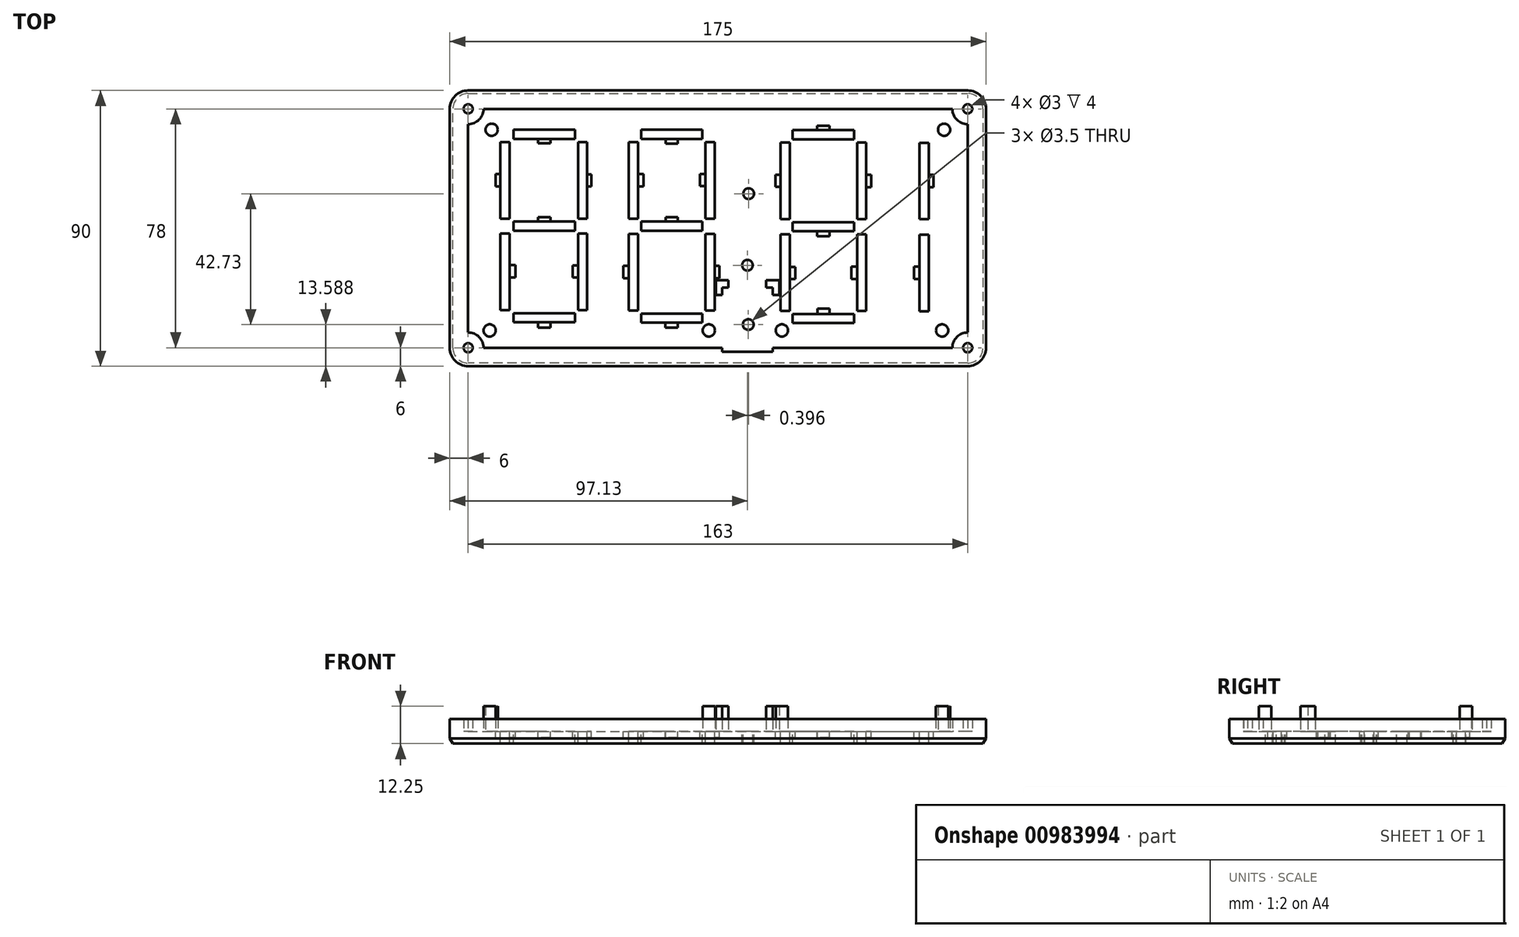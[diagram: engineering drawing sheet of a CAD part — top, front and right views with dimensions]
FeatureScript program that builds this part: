
annotation { "Feature Type Name" : "Feature", "Feature Type Description" : "" }
export const myFeature = defineFeature(function(context is Context, id is Id, definition is map)
    precondition{}
    {
        {
            var Q0;
            Q0=qCreatedBy(makeId("Top.planeOp"),FACE);
            var sketch = newSketch(context, id + "F0", { "sketchPlane" : qUnion([Q0])});
            skLineSegment(sketch, "E0.bottom", {"start": v(-87.5, 45) * mm, "end": v(87.5, 45) * mm});
            skLineSegment(sketch, "E0.top", {"start": v(-87.5, -45) * mm, "end": v(87.5, -45) * mm});
            skLineSegment(sketch, "E0.left", {"start": v(-87.5, 45) * mm, "end": v(-87.5, -45) * mm});
            skLineSegment(sketch, "E0.right", {"start": v(87.5, 45) * mm, "end": v(87.5, -45) * mm});
            skArc(sketch, "E1", {"start": v(-81.5, 34) * mm, "mid": v(-77.96, 35.46) * mm, "end": v(-76.5, 39) * mm});
            skArc(sketch, "E2", {"start": v(76.5, 39) * mm, "mid": v(77.96, 35.46) * mm, "end": v(81.5, 34) * mm});
            skArc(sketch, "E3", {"start": v(-76.5, -39) * mm, "mid": v(-77.96, -35.46) * mm, "end": v(-81.5, -34) * mm});
            skArc(sketch, "E4", {"start": v(81.5, -34) * mm, "mid": v(77.96, -35.46) * mm, "end": v(76.5, -39) * mm});
            skLineSegment(sketch, "E5", {"start": v(0, 39) * mm, "end": v(0, 0) * mm, "construction": true});
            skLineSegment(sketch, "E6.top", {"start": v(-68.01, -26.67) * mm, "end": v(-71.01, -26.67) * mm});
            skLineSegment(sketch, "E6.left", {"start": v(-68.01, -1.67) * mm, "end": v(-68.01, -26.67) * mm});
            skLineSegment(sketch, "E7.left", {"start": v(-68.01, 3.19) * mm, "end": v(-68.01, 28.19) * mm});
            skLineSegment(sketch, "E6.right", {"start": v(-71.01, -1.67) * mm, "end": v(-71.01, -26.67) * mm});
            skLineSegment(sketch, "E7.right", {"start": v(-71.01, 3.19) * mm, "end": v(-71.01, 28.19) * mm});
            skLineSegment(sketch, "E8.bottom", {"start": v(-45.68, -1.67) * mm, "end": v(-42.68, -1.67) * mm});
            skLineSegment(sketch, "E8.top", {"start": v(-45.68, -26.67) * mm, "end": v(-42.68, -26.67) * mm});
            skLineSegment(sketch, "E9.left", {"start": v(-46.68, 2.19) * mm, "end": v(-46.68, 29.19) * mm, "construction": true});
            skLineSegment(sketch, "E8.left", {"start": v(-45.68, -1.67) * mm, "end": v(-45.68, -26.67) * mm});
            skLineSegment(sketch, "E8.right", {"start": v(-42.68, -1.67) * mm, "end": v(-42.68, -26.67) * mm});
            skLineSegment(sketch, "E9.right", {"start": v(-41.68, 2.19) * mm, "end": v(-41.68, 29.19) * mm, "construction": true});
            skLineSegment(sketch, "E10", {"start": v(-45.68, -26.67) * mm, "end": v(-68.01, -26.67) * mm, "construction": true});
            skLineSegment(sketch, "E11.bottom", {"start": v(-46.68, -27.67) * mm, "end": v(-66.68, -27.67) * mm});
            skLineSegment(sketch, "E11.top", {"start": v(-46.68, -30.67) * mm, "end": v(-66.68, -30.67) * mm});
            skLineSegment(sketch, "E12.left", {"start": v(-66.68, 2.19) * mm, "end": v(-66.68, 29.19) * mm, "construction": true});
            skLineSegment(sketch, "E12.right", {"start": v(-72.01, 2.19) * mm, "end": v(-72.01, 29.19) * mm, "construction": true});
            skLineSegment(sketch, "E13.bottom", {"start": v(-46.68, 29.19) * mm, "end": v(-66.68, 29.19) * mm});
            skLineSegment(sketch, "E13.top", {"start": v(-46.68, 32.19) * mm, "end": v(-66.68, 32.19) * mm});
            skLineSegment(sketch, "E14.right", {"start": v(-42.68, 3.19) * mm, "end": v(-42.68, 28.19) * mm});
            skLineSegment(sketch, "E15.rect.bottom", {"start": v(-46.68, 2.19) * mm, "end": v(-66.68, 2.19) * mm});
            skLineSegment(sketch, "E15.rect.top", {"start": v(-46.68, -0.81) * mm, "end": v(-66.68, -0.81) * mm});
            skLineSegment(sketch, "E16.rect.bottom", {"start": v(-45.68, 3.19) * mm, "end": v(-68.01, 3.19) * mm, "construction": true});
            skLineSegment(sketch, "E16.rect.top", {"start": v(-45.68, -1.67) * mm, "end": v(-68.01, -1.67) * mm, "construction": true});
            skLineSegment(sketch, "E14.bottom", {"start": v(-45.68, 3.19) * mm, "end": v(-42.68, 3.19) * mm});
            skLineSegment(sketch, "E14.left", {"start": v(-45.68, 3.19) * mm, "end": v(-45.68, 28.19) * mm});
            skLineSegment(sketch, "E9.top", {"start": v(-46.68, 29.19) * mm, "end": v(-41.68, 29.19) * mm, "construction": true});
            skLineSegment(sketch, "E12.bottom", {"start": v(-66.68, 2.19) * mm, "end": v(-72.01, 2.19) * mm, "construction": true});
            skLineSegment(sketch, "E12.top", {"start": v(-66.68, 29.19) * mm, "end": v(-72.01, 29.19) * mm, "construction": true});
            skLineSegment(sketch, "E11.left", {"start": v(-46.68, -27.67) * mm, "end": v(-46.68, -30.67) * mm});
            skLineSegment(sketch, "E11.right", {"start": v(-66.68, -27.67) * mm, "end": v(-66.68, -30.67) * mm});
            skLineSegment(sketch, "E13.right", {"start": v(-66.68, 29.19) * mm, "end": v(-66.68, 32.19) * mm});
            skLineSegment(sketch, "E7.bottom", {"start": v(-68.01, 3.19) * mm, "end": v(-71.01, 3.19) * mm});
            skLineSegment(sketch, "E7.top", {"start": v(-68.01, 28.19) * mm, "end": v(-71.01, 28.19) * mm});
            skLineSegment(sketch, "E15.rect.left", {"start": v(-46.68, 2.19) * mm, "end": v(-46.68, -0.81) * mm});
            skLineSegment(sketch, "E15.rect.right", {"start": v(-66.68, 2.19) * mm, "end": v(-66.68, -0.81) * mm});
            skLineSegment(sketch, "E16.rect.right", {"start": v(-68.01, 3.19) * mm, "end": v(-68.01, -1.67) * mm, "construction": true});
            skLineSegment(sketch, "E13.left", {"start": v(-46.68, 29.19) * mm, "end": v(-46.68, 32.19) * mm});
            skLineSegment(sketch, "E14.top", {"start": v(-45.68, 28.19) * mm, "end": v(-42.68, 28.19) * mm});
            skLineSegment(sketch, "E6.bottom", {"start": v(-68.01, -1.67) * mm, "end": v(-71.01, -1.67) * mm});
            skLineSegment(sketch, "E9.bottom", {"start": v(-46.68, 2.19) * mm, "end": v(-41.68, 2.19) * mm, "construction": true});
            skLineSegment(sketch, "E16.rect.left", {"start": v(-45.68, 3.19) * mm, "end": v(-45.68, -1.67) * mm, "construction": true});
            skLineSegment(sketch, "E17.1.0.5", {"start": v(-5.06, -27.81) * mm, "end": v(-25.06, -27.81) * mm});
            skLineSegment(sketch, "E17.1.0.7", {"start": v(-4.06, -1.81) * mm, "end": v(-1.06, -1.81) * mm});
            skLineSegment(sketch, "E17.1.0.12", {"start": v(-4.06, 28.19) * mm, "end": v(-1.06, 28.19) * mm});
            skLineSegment(sketch, "E17.1.0.14", {"start": v(-4.06, 3.19) * mm, "end": v(-26.06, 3.19) * mm, "construction": true});
            skLineSegment(sketch, "E17.1.0.15", {"start": v(-26.06, -1.81) * mm, "end": v(-26.06, -26.81) * mm});
            skLineSegment(sketch, "E17.1.0.28", {"start": v(-5.06, -30.81) * mm, "end": v(-25.06, -30.81) * mm});
            skLineSegment(sketch, "E17.1.0.29", {"start": v(-1.06, -1.81) * mm, "end": v(-1.06, -26.81) * mm});
            skLineSegment(sketch, "E17.1.0.31", {"start": v(-4.06, -26.81) * mm, "end": v(-1.06, -26.81) * mm});
            skLineSegment(sketch, "E17.1.0.34", {"start": v(-26.06, 28.19) * mm, "end": v(-29.06, 28.19) * mm});
            skLineSegment(sketch, "E17.1.0.35", {"start": v(-5.06, 29.19) * mm, "end": v(-25.06, 29.19) * mm});
            skLineSegment(sketch, "E17.1.0.36", {"start": v(-29.06, -1.81) * mm, "end": v(-29.06, -26.81) * mm});
            skLineSegment(sketch, "E17.1.0.38", {"start": v(-5.06, 2.19) * mm, "end": v(-25.06, 2.19) * mm});
            skLineSegment(sketch, "E17.1.0.39", {"start": v(-26.06, -1.81) * mm, "end": v(-29.06, -1.81) * mm});
            skLineSegment(sketch, "E17.1.0.50", {"start": v(-4.06, -26.81) * mm, "end": v(-26.06, -26.81) * mm, "construction": true});
            skLineSegment(sketch, "E17.1.0.51", {"start": v(-4.06, -1.81) * mm, "end": v(-4.06, -26.81) * mm});
            skLineSegment(sketch, "E17.1.0.52", {"start": v(-5.06, 2.19) * mm, "end": v(-5.06, -0.81) * mm});
            skLineSegment(sketch, "E17.1.0.53", {"start": v(-4.06, 3.19) * mm, "end": v(-4.06, 28.19) * mm});
            skLineSegment(sketch, "E17.1.0.54", {"start": v(-5.06, 32.19) * mm, "end": v(-25.06, 32.19) * mm});
            skLineSegment(sketch, "E17.1.0.55", {"start": v(-29.06, 3.19) * mm, "end": v(-29.06, 28.19) * mm});
            skLineSegment(sketch, "E17.1.0.57", {"start": v(-30.06, 2.19) * mm, "end": v(-30.06, 29.19) * mm, "construction": true});
            skLineSegment(sketch, "E17.1.0.58", {"start": v(-4.06, -1.81) * mm, "end": v(-26.06, -1.81) * mm, "construction": true});
            skLineSegment(sketch, "E17.1.0.61", {"start": v(-26.06, 3.19) * mm, "end": v(-26.06, 28.19) * mm});
            skLineSegment(sketch, "E17.1.0.65", {"start": v(-25.06, 2.19) * mm, "end": v(-25.06, -0.81) * mm});
            skLineSegment(sketch, "E17.1.0.67", {"start": v(-1.06, 3.19) * mm, "end": v(-1.06, 28.19) * mm});
            skLineSegment(sketch, "E17.1.0.76", {"start": v(-25.06, 2.19) * mm, "end": v(-25.06, 29.19) * mm, "construction": true});
            skLineSegment(sketch, "E17.1.0.77", {"start": v(-5.06, -0.81) * mm, "end": v(-25.06, -0.81) * mm});
            skLineSegment(sketch, "E17.1.0.78", {"start": v(-0.06, 2.19) * mm, "end": v(-0.06, 29.19) * mm, "construction": true});
            skLineSegment(sketch, "E17.1.0.80", {"start": v(-5.06, 2.19) * mm, "end": v(-5.06, 29.19) * mm, "construction": true});
            skLineSegment(sketch, "E17.1.0.82", {"start": v(-5.06, -27.81) * mm, "end": v(-5.06, -30.81) * mm});
            skLineSegment(sketch, "E17.1.0.83", {"start": v(-26.06, -26.81) * mm, "end": v(-29.06, -26.81) * mm});
            skLineSegment(sketch, "E17.1.0.88", {"start": v(-5.06, 29.19) * mm, "end": v(-5.06, 32.19) * mm});
            skLineSegment(sketch, "E17.1.0.90", {"start": v(-25.06, -27.81) * mm, "end": v(-25.06, -30.81) * mm});
            skLineSegment(sketch, "E17.1.0.91", {"start": v(-5.06, 29.19) * mm, "end": v(-0.06, 29.19) * mm, "construction": true});
            skLineSegment(sketch, "E17.1.0.94", {"start": v(-5.06, 2.19) * mm, "end": v(-0.06, 2.19) * mm, "construction": true});
            skLineSegment(sketch, "E17.1.0.96", {"start": v(-4.06, 3.19) * mm, "end": v(-1.06, 3.19) * mm});
            skLineSegment(sketch, "E17.1.0.99", {"start": v(-26.06, 3.19) * mm, "end": v(-26.06, -1.81) * mm, "construction": true});
            skLineSegment(sketch, "E17.1.0.103", {"start": v(-26.06, 3.19) * mm, "end": v(-29.06, 3.19) * mm});
            skLineSegment(sketch, "E17.1.0.104", {"start": v(-25.06, 29.19) * mm, "end": v(-30.06, 29.19) * mm, "construction": true});
            skLineSegment(sketch, "E17.1.0.110", {"start": v(-25.06, 29.19) * mm, "end": v(-25.06, 32.19) * mm});
            skLineSegment(sketch, "E17.1.0.111", {"start": v(-25.06, 2.19) * mm, "end": v(-30.06, 2.19) * mm, "construction": true});
            skLineSegment(sketch, "E17.1.0.115", {"start": v(-4.06, 3.19) * mm, "end": v(-4.06, -1.81) * mm, "construction": true});
            skLineSegment(sketch, "E17.direction1", {"start": v(-42.68, 3.19) * mm, "end": v(-7.01, 3.19) * mm, "construction": true});
            skLineSegment(sketch, "E18.1.0.5", {"start": v(44.4, -27.96) * mm, "end": v(24.4, -27.96) * mm});
            skLineSegment(sketch, "E18.1.0.28", {"start": v(44.4, -30.96) * mm, "end": v(24.4, -30.96) * mm});
            skLineSegment(sketch, "E18.1.0.61", {"start": v(23.4, 3.04) * mm, "end": v(23.4, 28.04) * mm});
            skLineSegment(sketch, "E18.1.0.78", {"start": v(49.4, 2.04) * mm, "end": v(49.4, 29.04) * mm, "construction": true});
            skLineSegment(sketch, "E18.1.0.54", {"start": v(44.4, 32.04) * mm, "end": v(24.4, 32.04) * mm});
            skLineSegment(sketch, "E18.1.0.36", {"start": v(20.4, -1.96) * mm, "end": v(20.4, -26.96) * mm});
            skLineSegment(sketch, "E18.1.0.38", {"start": v(44.4, 2.04) * mm, "end": v(24.4, 2.04) * mm});
            skLineSegment(sketch, "E18.1.0.35", {"start": v(44.4, 29.04) * mm, "end": v(24.4, 29.04) * mm});
            skLineSegment(sketch, "E18.1.0.77", {"start": v(44.4, -0.96) * mm, "end": v(24.4, -0.96) * mm});
            skLineSegment(sketch, "E18.1.0.55", {"start": v(20.4, 3.04) * mm, "end": v(20.4, 28.04) * mm});
            skLineSegment(sketch, "E18.1.0.57", {"start": v(19.4, 2.04) * mm, "end": v(19.4, 29.04) * mm, "construction": true});
            skLineSegment(sketch, "E18.1.0.80", {"start": v(44.4, 2.04) * mm, "end": v(44.4, 29.04) * mm, "construction": true});
            skLineSegment(sketch, "E18.1.0.53", {"start": v(45.4, 3.04) * mm, "end": v(45.4, 28.04) * mm});
            skLineSegment(sketch, "E18.1.0.51", {"start": v(45.4, -1.96) * mm, "end": v(45.4, -26.96) * mm});
            skLineSegment(sketch, "E18.1.0.29", {"start": v(48.4, -1.96) * mm, "end": v(48.4, -26.96) * mm});
            skLineSegment(sketch, "E18.1.0.76", {"start": v(24.4, 2.04) * mm, "end": v(24.4, 29.04) * mm, "construction": true});
            skLineSegment(sketch, "E18.1.0.67", {"start": v(48.4, 3.04) * mm, "end": v(48.4, 28.04) * mm});
            skLineSegment(sketch, "E18.1.0.50", {"start": v(45.4, -26.96) * mm, "end": v(23.4, -26.96) * mm, "construction": true});
            skLineSegment(sketch, "E18.1.0.58", {"start": v(45.4, -1.96) * mm, "end": v(23.4, -1.96) * mm, "construction": true});
            skLineSegment(sketch, "E18.1.0.15", {"start": v(23.4, -1.96) * mm, "end": v(23.4, -26.96) * mm});
            skLineSegment(sketch, "E18.1.0.14", {"start": v(45.4, 3.04) * mm, "end": v(23.4, 3.04) * mm, "construction": true});
            skLineSegment(sketch, "E18.1.0.12", {"start": v(45.4, 28.04) * mm, "end": v(48.4, 28.04) * mm});
            skLineSegment(sketch, "E18.1.0.91", {"start": v(44.4, 29.04) * mm, "end": v(49.4, 29.04) * mm, "construction": true});
            skLineSegment(sketch, "E18.1.0.90", {"start": v(24.4, -27.96) * mm, "end": v(24.4, -30.96) * mm});
            skLineSegment(sketch, "E18.1.0.111", {"start": v(24.4, 2.04) * mm, "end": v(19.4, 2.04) * mm, "construction": true});
            skLineSegment(sketch, "E18.1.0.34", {"start": v(23.4, 28.04) * mm, "end": v(20.4, 28.04) * mm});
            skLineSegment(sketch, "E18.1.0.104", {"start": v(24.4, 29.04) * mm, "end": v(19.4, 29.04) * mm, "construction": true});
            skLineSegment(sketch, "E18.1.0.82", {"start": v(44.4, -27.96) * mm, "end": v(44.4, -30.96) * mm});
            skLineSegment(sketch, "E18.1.0.94", {"start": v(44.4, 2.04) * mm, "end": v(49.4, 2.04) * mm, "construction": true});
            skLineSegment(sketch, "E18.1.0.31", {"start": v(45.4, -26.96) * mm, "end": v(48.4, -26.96) * mm});
            skLineSegment(sketch, "E18.1.0.83", {"start": v(23.4, -26.96) * mm, "end": v(20.4, -26.96) * mm});
            skLineSegment(sketch, "E18.1.0.88", {"start": v(44.4, 29.04) * mm, "end": v(44.4, 32.04) * mm});
            skLineSegment(sketch, "E18.1.0.96", {"start": v(45.4, 3.04) * mm, "end": v(48.4, 3.04) * mm});
            skLineSegment(sketch, "E18.1.0.103", {"start": v(23.4, 3.04) * mm, "end": v(20.4, 3.04) * mm});
            skLineSegment(sketch, "E18.1.0.99", {"start": v(23.4, 3.04) * mm, "end": v(23.4, -1.96) * mm, "construction": true});
            skLineSegment(sketch, "E18.1.0.7", {"start": v(45.4, -1.96) * mm, "end": v(48.4, -1.96) * mm});
            skLineSegment(sketch, "E18.1.0.115", {"start": v(45.4, 3.04) * mm, "end": v(45.4, -1.96) * mm, "construction": true});
            skLineSegment(sketch, "E18.1.0.52", {"start": v(44.4, 2.04) * mm, "end": v(44.4, -0.96) * mm});
            skLineSegment(sketch, "E18.1.0.110", {"start": v(24.4, 29.04) * mm, "end": v(24.4, 32.04) * mm});
            skLineSegment(sketch, "E18.1.0.65", {"start": v(24.4, 2.04) * mm, "end": v(24.4, -0.96) * mm});
            skLineSegment(sketch, "E18.1.0.39", {"start": v(23.4, -1.96) * mm, "end": v(20.4, -1.96) * mm});
            skLineSegment(sketch, "E19.1.0.51", {"start": v(65.76, -2.04) * mm, "end": v(65.76, -27.04) * mm});
            skLineSegment(sketch, "E19.1.0.29", {"start": v(68.76, -2.04) * mm, "end": v(68.76, -27.04) * mm});
            skLineSegment(sketch, "E19.1.0.53", {"start": v(65.76, 2.96) * mm, "end": v(65.76, 27.96) * mm});
            skLineSegment(sketch, "E19.1.0.78", {"start": v(69.76, 1.96) * mm, "end": v(69.76, 28.96) * mm, "construction": true});
            skLineSegment(sketch, "E19.1.0.67", {"start": v(68.76, 2.96) * mm, "end": v(68.76, 27.96) * mm});
            skLineSegment(sketch, "E19.1.0.80", {"start": v(64.76, 1.96) * mm, "end": v(64.76, 28.96) * mm, "construction": true});
            skLineSegment(sketch, "E19.1.0.31", {"start": v(65.76, -27.04) * mm, "end": v(68.76, -27.04) * mm});
            skLineSegment(sketch, "E19.1.0.96", {"start": v(65.76, 2.96) * mm, "end": v(68.76, 2.96) * mm});
            skLineSegment(sketch, "E19.1.0.12", {"start": v(65.76, 27.96) * mm, "end": v(68.76, 27.96) * mm});
            skLineSegment(sketch, "E19.1.0.94", {"start": v(64.76, 1.96) * mm, "end": v(69.76, 1.96) * mm, "construction": true});
            skLineSegment(sketch, "E19.1.0.7", {"start": v(65.76, -2.04) * mm, "end": v(68.76, -2.04) * mm});
            skLineSegment(sketch, "E19.1.0.91", {"start": v(64.76, 28.96) * mm, "end": v(69.76, 28.96) * mm, "construction": true});
            skLineSegment(sketch, "E19.1.0.115", {"start": v(65.76, 2.96) * mm, "end": v(65.76, -2.04) * mm, "construction": true});
            skLineSegment(sketch, "E20", {"start": v(-66.68, 32.19) * mm, "end": v(77.46, 32.19) * mm, "construction": true});
            skLineSegment(sketch, "E21", {"start": v(50.1, 29.04) * mm, "end": v(77.85, 29.04) * mm, "construction": true});
            skCircle(sketch, "E22", {"center": v(9.63, -12.05) * mm, "radius": 1.75 * mm});
            skCircle(sketch, "E23", {"center": v(10.03, 11.32) * mm, "radius": 1.75 * mm});
            skCircle(sketch, "E24", {"center": v(-81.5, 39) * mm, "radius": 1.5 * mm});
            skCircle(sketch, "E25", {"center": v(-81.5, -39) * mm, "radius": 1.5 * mm});
            skCircle(sketch, "E26", {"center": v(81.5, -39) * mm, "radius": 1.5 * mm});
            skCircle(sketch, "E27", {"center": v(81.5, 39) * mm, "radius": 1.5 * mm});
            skLineSegment(sketch, "E28.trimOffspring", {"start": v(81.5, 34) * mm, "end": v(81.5, -34) * mm});
            skLineSegment(sketch, "E29.trimOffspring", {"start": v(-76.5, -39) * mm, "end": v(17.9, -39) * mm});
            skLineSegment(sketch, "E30.trimOffspring", {"start": v(-81.5, 34) * mm, "end": v(-81.5, -34) * mm});
            skLineSegment(sketch, "E31.trimOffspring", {"start": v(-76.5, 39) * mm, "end": v(76.5, 39) * mm});
            skLineSegment(sketch, "E32.rect.bottom", {"start": v(17.9, -40.3) * mm, "end": v(1.4, -40.3) * mm});
            skLineSegment(sketch, "E32.rect.top", {"start": v(17.9, -19.35) * mm, "end": v(15.73, -19.35) * mm});
            skLineSegment(sketch, "E32.rect.left", {"start": v(17.9, -40.3) * mm, "end": v(17.9, -39) * mm});
            skLineSegment(sketch, "E32.rect.right", {"start": v(1.4, -40.3) * mm, "end": v(1.4, -39) * mm});
            skPoint(sketch, "E32.rect.middle", {"position": v(9.65, -29.82) * mm});
            skCircle(sketch, "E33", {"center": v(9.9, -31.41) * mm, "radius": 1.75 * mm});
            skLineSegment(sketch, "E34.rect.bottom", {"start": v(17.9, -21.72) * mm, "end": v(20.08, -21.72) * mm});
            skLineSegment(sketch, "E34.rect.top", {"start": v(15.73, -16.98) * mm, "end": v(20.08, -16.98) * mm});
            skLineSegment(sketch, "E34.rect.left", {"start": v(15.73, -19.35) * mm, "end": v(15.73, -16.98) * mm});
            skLineSegment(sketch, "E34.rect.right", {"start": v(20.08, -21.72) * mm, "end": v(20.08, -16.98) * mm});
            skPoint(sketch, "E34.rect.middle", {"position": v(17.9, -19.35) * mm});
            skLineSegment(sketch, "E35.rect.bottom", {"start": v(1.4, -21.72) * mm, "end": v(-0.6, -21.72) * mm});
            skLineSegment(sketch, "E35.rect.top", {"start": v(3.4, -16.98) * mm, "end": v(-0.6, -16.98) * mm});
            skLineSegment(sketch, "E35.rect.left", {"start": v(3.4, -19.35) * mm, "end": v(3.4, -16.98) * mm});
            skLineSegment(sketch, "E35.rect.right", {"start": v(-0.6, -21.72) * mm, "end": v(-0.6, -16.98) * mm});
            skPoint(sketch, "E35.rect.middle", {"position": v(1.4, -19.35) * mm});
            skPoint(sketch, "E36.orphan", {"position": v(3.4, -21.72) * mm});
            skPoint(sketch, "E37.orphan", {"position": v(15.73, -21.72) * mm});
            skLineSegment(sketch, "E38", {"start": v(3.4, -19.35) * mm, "end": v(1.4, -19.35) * mm});
            skLineSegment(sketch, "E39", {"start": v(15.73, -19.35) * mm, "end": v(3.4, -19.35) * mm, "construction": true});
            skLineSegment(sketch, "E40", {"start": v(1.4, -21.72) * mm, "end": v(1.4, -19.35) * mm});
            skLineSegment(sketch, "E41", {"start": v(17.9, -21.72) * mm, "end": v(17.9, -19.35) * mm});
            skLineSegment(sketch, "E42", {"start": v(17.9, -39) * mm, "end": v(76.5, -39) * mm});
            skLineSegment(sketch, "E43", {"start": v(1.4, -39) * mm, "end": v(1.4, -21.72) * mm, "construction": true});
            skLineSegment(sketch, "E44", {"start": v(17.9, -39) * mm, "end": v(17.9, -21.72) * mm, "construction": true});
            skCircle(sketch, "E45", {"center": v(73.8, 32.19) * mm, "radius": 2 * mm});
            skCircle(sketch, "E46", {"center": v(73.15, -33.33) * mm, "radius": 2 * mm});
            skCircle(sketch, "E47", {"center": v(-73.84, 32.19) * mm, "radius": 2 * mm});
            skCircle(sketch, "E48", {"center": v(-74.5, -33.33) * mm, "radius": 2 * mm});
            skCircle(sketch, "E49", {"center": v(20.87, -33.33) * mm, "radius": 2 * mm});
            skCircle(sketch, "E50", {"center": v(-2.98, -33.33) * mm, "radius": 2 * mm});
            skLineSegment(sketch, "E51.rect.bottom", {"start": v(-66.1, -16.02) * mm, "end": v(-68.01, -16.02) * mm});
            skLineSegment(sketch, "E51.rect.top", {"start": v(-66.1, -12.02) * mm, "end": v(-68.01, -12.02) * mm});
            skLineSegment(sketch, "E51.rect.left", {"start": v(-66.1, -16.02) * mm, "end": v(-66.1, -12.02) * mm});
            skLineSegment(sketch, "E52.rect.bottom", {"start": v(-47.39, -16.1) * mm, "end": v(-45.68, -16.1) * mm});
            skLineSegment(sketch, "E52.rect.top", {"start": v(-47.39, -12.1) * mm, "end": v(-45.68, -12.1) * mm});
            skLineSegment(sketch, "E52.rect.left", {"start": v(-47.39, -16.1) * mm, "end": v(-47.39, -12.1) * mm});
            skLineSegment(sketch, "E53.rect.bottom", {"start": v(-58.68, -32.37) * mm, "end": v(-54.68, -32.37) * mm});
            skLineSegment(sketch, "E53.rect.left", {"start": v(-58.68, -32.37) * mm, "end": v(-58.68, -30.67) * mm});
            skLineSegment(sketch, "E53.rect.right", {"start": v(-54.68, -32.37) * mm, "end": v(-54.68, -30.67) * mm});
            skLineSegment(sketch, "E54.rect.bottom", {"start": v(-58.68, 3.68) * mm, "end": v(-54.68, 3.68) * mm});
            skLineSegment(sketch, "E54.rect.left", {"start": v(-58.68, 3.68) * mm, "end": v(-58.68, 2.19) * mm});
            skLineSegment(sketch, "E54.rect.right", {"start": v(-54.68, 3.68) * mm, "end": v(-54.68, 2.19) * mm});
            skLineSegment(sketch, "E55.rect.bottom", {"start": v(-72.53, 13.69) * mm, "end": v(-71.01, 13.69) * mm});
            skLineSegment(sketch, "E55.rect.top", {"start": v(-72.53, 17.69) * mm, "end": v(-71.01, 17.69) * mm});
            skLineSegment(sketch, "E55.rect.left", {"start": v(-72.53, 13.69) * mm, "end": v(-72.53, 17.69) * mm});
            skLineSegment(sketch, "E56.rect.bottom", {"start": v(-58.68, 27.77) * mm, "end": v(-54.68, 27.77) * mm});
            skLineSegment(sketch, "E56.rect.left", {"start": v(-58.68, 27.77) * mm, "end": v(-58.68, 29.19) * mm});
            skLineSegment(sketch, "E56.rect.right", {"start": v(-54.68, 27.77) * mm, "end": v(-54.68, 29.19) * mm});
            skLineSegment(sketch, "E57.rect.bottom", {"start": v(-41.3, 17.68) * mm, "end": v(-42.68, 17.68) * mm});
            skLineSegment(sketch, "E57.rect.top", {"start": v(-41.3, 13.68) * mm, "end": v(-42.68, 13.68) * mm});
            skLineSegment(sketch, "E57.rect.left", {"start": v(-41.3, 17.68) * mm, "end": v(-41.3, 13.68) * mm});
            skLineSegment(sketch, "E58.rect.bottom", {"start": v(-17.1, 27.61) * mm, "end": v(-13.1, 27.61) * mm});
            skLineSegment(sketch, "E58.rect.left", {"start": v(-17.1, 27.61) * mm, "end": v(-17.1, 29.19) * mm});
            skLineSegment(sketch, "E58.rect.right", {"start": v(-13.1, 27.61) * mm, "end": v(-13.1, 29.19) * mm});
            skLineSegment(sketch, "E59.rect.bottom", {"start": v(-24.23, 17.69) * mm, "end": v(-26.06, 17.69) * mm});
            skLineSegment(sketch, "E59.rect.top", {"start": v(-24.23, 13.69) * mm, "end": v(-26.06, 13.69) * mm});
            skLineSegment(sketch, "E59.rect.left", {"start": v(-24.23, 17.69) * mm, "end": v(-24.23, 13.69) * mm});
            skLineSegment(sketch, "E60.rect.bottom", {"start": v(-5.85, 13.78) * mm, "end": v(-4.06, 13.78) * mm});
            skLineSegment(sketch, "E60.rect.top", {"start": v(-5.85, 17.78) * mm, "end": v(-4.06, 17.78) * mm});
            skLineSegment(sketch, "E60.rect.left", {"start": v(-5.85, 13.78) * mm, "end": v(-5.85, 17.78) * mm});
            skLineSegment(sketch, "E61.rect.bottom", {"start": v(-17.1, 3.6) * mm, "end": v(-13.1, 3.6) * mm});
            skLineSegment(sketch, "E61.rect.left", {"start": v(-17.1, 3.6) * mm, "end": v(-17.1, 2.19) * mm});
            skLineSegment(sketch, "E61.rect.right", {"start": v(-13.1, 3.6) * mm, "end": v(-13.1, 2.19) * mm});
            skLineSegment(sketch, "E62.rect.bottom", {"start": v(-30.88, -12.29) * mm, "end": v(-29.06, -12.29) * mm});
            skLineSegment(sketch, "E62.rect.top", {"start": v(-30.88, -16.29) * mm, "end": v(-29.06, -16.29) * mm});
            skLineSegment(sketch, "E62.rect.left", {"start": v(-30.88, -12.29) * mm, "end": v(-30.88, -16.29) * mm});
            skLineSegment(sketch, "E63.rect.bottom", {"start": v(0.5, -12.23) * mm, "end": v(-1.06, -12.23) * mm});
            skLineSegment(sketch, "E63.rect.top", {"start": v(0.5, -16.23) * mm, "end": v(-1.06, -16.23) * mm});
            skLineSegment(sketch, "E63.rect.left", {"start": v(0.5, -12.23) * mm, "end": v(0.5, -16.23) * mm});
            skLineSegment(sketch, "E64.rect.bottom", {"start": v(-17.16, -32.42) * mm, "end": v(-13.16, -32.42) * mm});
            skLineSegment(sketch, "E64.rect.left", {"start": v(-17.16, -32.42) * mm, "end": v(-17.16, -30.81) * mm});
            skLineSegment(sketch, "E64.rect.right", {"start": v(-13.16, -32.42) * mm, "end": v(-13.16, -30.81) * mm});
            skLineSegment(sketch, "E65.rect.bottom", {"start": v(32.4, 33.52) * mm, "end": v(36.4, 33.52) * mm});
            skLineSegment(sketch, "E65.rect.left", {"start": v(32.4, 33.52) * mm, "end": v(32.4, 32.04) * mm});
            skLineSegment(sketch, "E65.rect.right", {"start": v(36.4, 33.52) * mm, "end": v(36.4, 32.04) * mm});
            skLineSegment(sketch, "E66.rect.bottom", {"start": v(18.75, 13.55) * mm, "end": v(20.4, 13.55) * mm});
            skLineSegment(sketch, "E66.rect.top", {"start": v(18.75, 17.55) * mm, "end": v(20.4, 17.55) * mm});
            skLineSegment(sketch, "E66.rect.left", {"start": v(18.75, 13.55) * mm, "end": v(18.75, 17.55) * mm});
            skLineSegment(sketch, "E67.rect.bottom", {"start": v(50, 17.48) * mm, "end": v(48.4, 17.48) * mm});
            skLineSegment(sketch, "E67.rect.top", {"start": v(50, 13.48) * mm, "end": v(48.4, 13.48) * mm});
            skLineSegment(sketch, "E67.rect.left", {"start": v(50, 17.48) * mm, "end": v(50, 13.48) * mm});
            skLineSegment(sketch, "E68.rect.bottom", {"start": v(32.38, -2.53) * mm, "end": v(36.38, -2.53) * mm});
            skLineSegment(sketch, "E68.rect.left", {"start": v(32.38, -2.53) * mm, "end": v(32.38, -0.96) * mm});
            skLineSegment(sketch, "E68.rect.right", {"start": v(36.38, -2.53) * mm, "end": v(36.38, -0.96) * mm});
            skLineSegment(sketch, "E69.rect.bottom", {"start": v(25.28, -12.57) * mm, "end": v(23.4, -12.57) * mm});
            skLineSegment(sketch, "E69.rect.top", {"start": v(25.28, -16.57) * mm, "end": v(23.4, -16.57) * mm});
            skLineSegment(sketch, "E69.rect.left", {"start": v(25.28, -12.57) * mm, "end": v(25.28, -16.57) * mm});
            skLineSegment(sketch, "E70.rect.bottom", {"start": v(43.49, -16.54) * mm, "end": v(45.4, -16.54) * mm});
            skLineSegment(sketch, "E70.rect.top", {"start": v(43.49, -12.54) * mm, "end": v(45.4, -12.54) * mm});
            skLineSegment(sketch, "E70.rect.left", {"start": v(43.49, -16.54) * mm, "end": v(43.49, -12.54) * mm});
            skLineSegment(sketch, "E71.rect.bottom", {"start": v(36.43, -26.21) * mm, "end": v(32.43, -26.21) * mm});
            skLineSegment(sketch, "E71.rect.left", {"start": v(36.43, -26.21) * mm, "end": v(36.43, -27.96) * mm});
            skLineSegment(sketch, "E71.rect.right", {"start": v(32.43, -26.21) * mm, "end": v(32.43, -27.96) * mm});
            skLineSegment(sketch, "E72.rect.bottom", {"start": v(68.76, 17.48) * mm, "end": v(70.36, 17.48) * mm});
            skLineSegment(sketch, "E72.rect.top", {"start": v(68.76, 13.45) * mm, "end": v(70.36, 13.45) * mm});
            skLineSegment(sketch, "E72.rect.right", {"start": v(70.36, 17.48) * mm, "end": v(70.36, 13.45) * mm});
            skLineSegment(sketch, "E73.rect.bottom", {"start": v(63.96, -12.54) * mm, "end": v(65.76, -12.54) * mm});
            skLineSegment(sketch, "E73.rect.top", {"start": v(63.96, -16.53) * mm, "end": v(65.76, -16.53) * mm});
            skLineSegment(sketch, "E73.rect.left", {"start": v(63.96, -12.54) * mm, "end": v(63.96, -16.53) * mm});
            skSolve(sketch);
        }
        {
            var Q0;
            Q0=makeQuery(id+"F0.imprint","IMPRINT",FACE,{"disambiguationData":[TD([[makeQuery(id+"F0.imprint","IMPRINT",EDGE,{"derivedFrom":sQuery(id+"F0.wireOp",EDGE,"E0.bottom")}),-1.0]])]});
            var Q1;
            Q1=makeQuery(id+"F0.imprint","IMPRINT",FACE,{"disambiguationData":[TD([[makeQuery(id+"F0.imprint","IMPRINT",EDGE,{"derivedFrom":sQuery(id+"F0.wireOp",EDGE,"E17.1.0.5")}),1.0]])]});
            var Q2;
            {var subQ7=sQuery(id+"F0.wireOp",EDGE,"E17.1.0.12");Q2=makeQuery(id+"F0.imprint","IMPRINT",FACE,{"disambiguationData":[TD([[makeQuery(id+"F0.imprint","IMPRINT",EDGE,{"derivedFrom":subQ7}),-1.0]])]});}
            var Q3;
            {var subQ7=sQuery(id+"F0.wireOp",EDGE,"E17.1.0.7");Q3=makeQuery(id+"F0.imprint","IMPRINT",FACE,{"disambiguationData":[TD([[makeQuery(id+"F0.imprint","IMPRINT",EDGE,{"derivedFrom":subQ7}),-1.0]])]});}
            var Q4;
            Q4=makeQuery(id+"F0.imprint","IMPRINT",FACE,{"disambiguationData":[TD([[makeQuery(id+"F0.imprint","IMPRINT",EDGE,{"derivedFrom":sQuery(id+"F0.wireOp",EDGE,"E11.bottom")}),1.0]])]});
            var Q5;
            Q5=makeQuery(id+"F0.imprint","IMPRINT",FACE,{"disambiguationData":[TD([[makeQuery(id+"F0.imprint","IMPRINT",EDGE,{"derivedFrom":sQuery(id+"F0.wireOp",EDGE,"E18.1.0.38")}),1.0]])]});
            var Q6;
            Q6=makeQuery(id+"F0.imprint","IMPRINT",FACE,{"disambiguationData":[TD([[makeQuery(id+"F0.imprint","IMPRINT",EDGE,{"derivedFrom":sQuery(id+"F0.wireOp",EDGE,"E18.1.0.29")}),-1.0]])]});
            var Q7;
            Q7=makeQuery(id+"F0.imprint","IMPRINT",FACE,{"disambiguationData":[TD([[makeQuery(id+"F0.imprint","IMPRINT",EDGE,{"derivedFrom":sQuery(id+"F0.wireOp",EDGE,"E18.1.0.28")}),-1.0]])]});
            var Q8;
            {var subQ7=sQuery(id+"F0.wireOp",EDGE,"E6.top");Q8=makeQuery(id+"F0.imprint","IMPRINT",FACE,{"disambiguationData":[TD([[makeQuery(id+"F0.imprint","IMPRINT",EDGE,{"derivedFrom":subQ7}),-1.0]])]});}
            var Q9;
            Q9=makeQuery(id+"F0.imprint","IMPRINT",FACE,{"disambiguationData":[TD([[makeQuery(id+"F0.imprint","IMPRINT",EDGE,{"derivedFrom":sQuery(id+"F0.wireOp",EDGE,"E7.left")}),1.0]])]});
            var Q10;
            {var subQ7=sQuery(id+"F0.wireOp",EDGE,"E8.bottom");Q10=makeQuery(id+"F0.imprint","IMPRINT",FACE,{"disambiguationData":[TD([[makeQuery(id+"F0.imprint","IMPRINT",EDGE,{"derivedFrom":subQ7}),-1.0]])]});}
            var Q11;
            Q11=makeQuery(id+"F0.imprint","IMPRINT",FACE,{"disambiguationData":[TD([[makeQuery(id+"F0.imprint","IMPRINT",EDGE,{"derivedFrom":sQuery(id+"F0.wireOp",EDGE,"E13.top")}),1.0]])]});
            var Q12;
            {var subQ7=sQuery(id+"F0.wireOp",EDGE,"E14.bottom");Q12=makeQuery(id+"F0.imprint","IMPRINT",FACE,{"disambiguationData":[TD([[makeQuery(id+"F0.imprint","IMPRINT",EDGE,{"derivedFrom":subQ7}),1.0]])]});}
            var Q13;
            Q13=makeQuery(id+"F0.imprint","IMPRINT",FACE,{"disambiguationData":[TD([[makeQuery(id+"F0.imprint","IMPRINT",EDGE,{"derivedFrom":sQuery(id+"F0.wireOp",EDGE,"E15.rect.top")}),-1.0]])]});
            var Q14;
            Q14=makeQuery(id+"F0.imprint","IMPRINT",FACE,{"disambiguationData":[TD([[makeQuery(id+"F0.imprint","IMPRINT",EDGE,{"derivedFrom":sQuery(id+"F0.wireOp",EDGE,"E19.1.0.53")}),-1.0]])]});
            var Q15;
            Q15=makeQuery(id+"F0.imprint","IMPRINT",FACE,{"disambiguationData":[TD([[makeQuery(id+"F0.imprint","IMPRINT",EDGE,{"derivedFrom":sQuery(id+"F0.wireOp",EDGE,"E18.1.0.61")}),1.0]])]});
            var Q16;
            {var subQ7=sQuery(id+"F0.wireOp",EDGE,"E17.1.0.52");Q16=makeQuery(id+"F0.imprint","IMPRINT",FACE,{"disambiguationData":[TD([[makeQuery(id+"F0.imprint","IMPRINT",EDGE,{"derivedFrom":subQ7}),-1.0]])]});}
            var Q17;
            Q17=makeQuery(id+"F0.imprint","IMPRINT",FACE,{"disambiguationData":[TD([[makeQuery(id+"F0.imprint","IMPRINT",EDGE,{"derivedFrom":sQuery(id+"F0.wireOp",EDGE,"E1")}),-1.0]])]});
            var Q18;
            Q18=makeQuery(id+"F0.imprint","IMPRINT",FACE,{"disambiguationData":[TD([[makeQuery(id+"F0.imprint","IMPRINT",EDGE,{"derivedFrom":sQuery(id+"F0.wireOp",EDGE,"E18.1.0.36")}),1.0]])]});
            var Q19;
            Q19=makeQuery(id+"F0.imprint","IMPRINT",FACE,{"disambiguationData":[TD([[makeQuery(id+"F0.imprint","IMPRINT",EDGE,{"derivedFrom":sQuery(id+"F0.wireOp",EDGE,"E17.1.0.54")}),1.0]])]});
            var Q20;
            Q20=makeQuery(id+"F0.imprint","IMPRINT",FACE,{"disambiguationData":[TD([[makeQuery(id+"F0.imprint","IMPRINT",EDGE,{"derivedFrom":sQuery(id+"F0.wireOp",EDGE,"E19.1.0.29")}),-1.0]])]});
            var Q21;
            Q21=makeQuery(id+"F0.imprint","IMPRINT",FACE,{"disambiguationData":[TD([[makeQuery(id+"F0.imprint","IMPRINT",EDGE,{"derivedFrom":sQuery(id+"F0.wireOp",EDGE,"E17.1.0.15")}),-1.0]])]});
            var Q22;
            {var subQ6=sQuery(id+"F0.wireOp",EDGE,"E17.1.0.34");Q22=makeQuery(id+"F0.imprint","IMPRINT",FACE,{"disambiguationData":[TD([[makeQuery(id+"F0.imprint","IMPRINT",EDGE,{"derivedFrom":subQ6}),1.0]])]});}
            var Q23;
            Q23=makeQuery(id+"F0.imprint","IMPRINT",FACE,{"disambiguationData":[TD([[makeQuery(id+"F0.imprint","IMPRINT",EDGE,{"derivedFrom":sQuery(id+"F0.wireOp",EDGE,"E18.1.0.53")}),-1.0]])]});
            var Q24;
            Q24=makeQuery(id+"F0.imprint","IMPRINT",FACE,{"disambiguationData":[TD([[makeQuery(id+"F0.imprint","IMPRINT",EDGE,{"derivedFrom":sQuery(id+"F0.wireOp",EDGE,"E18.1.0.35")}),-1.0]])]});
            var Q25;
            Q25=makeQuery(id+"F0.imprint","IMPRINT",FACE,{"disambiguationData":[TD([[makeQuery(id+"F0.imprint","IMPRINT",EDGE,{"derivedFrom":sQuery(id+"F0.wireOp",EDGE,"E22")}),1.0]])]});
            var Q26;
            Q26=makeQuery(id+"F0.imprint","IMPRINT",FACE,{"disambiguationData":[TD([[makeQuery(id+"F0.imprint","IMPRINT",EDGE,{"derivedFrom":sQuery(id+"F0.wireOp",EDGE,"E23")}),1.0]])]});
            var Q27;
            Q27=makeQuery(id+"F0.imprint","IMPRINT",FACE,{"disambiguationData":[TD([[makeQuery(id+"F0.imprint","IMPRINT",EDGE,{"derivedFrom":sQuery(id+"F0.wireOp",EDGE,"E24")}),1.0]])]});
            var Q28;
            Q28=makeQuery(id+"F0.imprint","IMPRINT",FACE,{"disambiguationData":[TD([[makeQuery(id+"F0.imprint","IMPRINT",EDGE,{"derivedFrom":sQuery(id+"F0.wireOp",EDGE,"E25")}),1.0]])]});
            var Q29;
            Q29=makeQuery(id+"F0.imprint","IMPRINT",FACE,{"disambiguationData":[TD([[makeQuery(id+"F0.imprint","IMPRINT",EDGE,{"derivedFrom":sQuery(id+"F0.wireOp",EDGE,"E26")}),1.0]])]});
            var Q30;
            Q30=makeQuery(id+"F0.imprint","IMPRINT",FACE,{"disambiguationData":[TD([[makeQuery(id+"F0.imprint","IMPRINT",EDGE,{"derivedFrom":sQuery(id+"F0.wireOp",EDGE,"E27")}),1.0]])]});
            var Q31;
            {var subQ3=sQuery(id+"F0.wireOp",EDGE,"d27d8e91-9dc8-4657-a3bc-17c214d1fbd1.rect.top");Q31=makeQuery(id+"F0.imprint","IMPRINT",FACE,{"disambiguationData":[TD([[makeQuery(id+"F0.imprint","IMPRINT",EDGE,{"derivedFrom":subQ3}),1.0]])]});}
            var Q32;
            {var subQ3=sQuery(id+"F0.wireOp",EDGE,"d27d8e91-9dc8-4657-a3bc-17c214d1fbd1.rect.bottom");Q32=makeQuery(id+"F0.imprint","IMPRINT",FACE,{"disambiguationData":[TD([[makeQuery(id+"F0.imprint","IMPRINT",EDGE,{"derivedFrom":subQ3}),-1.0]])]});}
            var Q33;
            {var subQ0=sQuery(id+"F0.wireOp",EDGE,"11542846-51ec-4e1d-9889-e9b2482069cd.rect.left");Q33=makeQuery(id+"F0.imprint","IMPRINT",FACE,{"disambiguationData":[TD([[makeQuery(id+"F0.imprint","IMPRINT",EDGE,{"derivedFrom":subQ0}),-1.0]])]});}
            var Q34;
            {var subQ0=sQuery(id+"F0.wireOp",EDGE,"11542846-51ec-4e1d-9889-e9b2482069cd.rect.right");Q34=makeQuery(id+"F0.imprint","IMPRINT",FACE,{"disambiguationData":[TD([[makeQuery(id+"F0.imprint","IMPRINT",EDGE,{"derivedFrom":subQ0}),1.0]])]});}
            var Q35;
            {var subQ0=sQuery(id+"F0.wireOp",EDGE,"7a176b9b-9b07-41be-aea8-fdd94f8c28c8.rect.right");Q35=makeQuery(id+"F0.imprint","IMPRINT",FACE,{"disambiguationData":[TD([[makeQuery(id+"F0.imprint","IMPRINT",EDGE,{"derivedFrom":subQ0}),1.0]])]});}
            var Q36;
            {var subQ0=sQuery(id+"F0.wireOp",EDGE,"7a176b9b-9b07-41be-aea8-fdd94f8c28c8.rect.left");Q36=makeQuery(id+"F0.imprint","IMPRINT",FACE,{"disambiguationData":[TD([[makeQuery(id+"F0.imprint","IMPRINT",EDGE,{"derivedFrom":subQ0}),-1.0]])]});}
            var Q37;
            {var subQ0=sQuery(id+"F0.wireOp",EDGE,"7fec9149-b94b-4e31-a2bc-72143b81982d.rect.right");Q37=makeQuery(id+"F0.imprint","IMPRINT",FACE,{"disambiguationData":[TD([[makeQuery(id+"F0.imprint","IMPRINT",EDGE,{"derivedFrom":subQ0}),-1.0]])]});}
            var Q38;
            {var subQ0=sQuery(id+"F0.wireOp",EDGE,"7fec9149-b94b-4e31-a2bc-72143b81982d.rect.left");Q38=makeQuery(id+"F0.imprint","IMPRINT",FACE,{"disambiguationData":[TD([[makeQuery(id+"F0.imprint","IMPRINT",EDGE,{"derivedFrom":subQ0}),1.0]])]});}
            var Q39;
            {var subQ3=sQuery(id+"F0.wireOp",EDGE,"2390580b-736b-4805-a3aa-b3ade61d923c.rect.bottom");Q39=makeQuery(id+"F0.imprint","IMPRINT",FACE,{"disambiguationData":[TD([[makeQuery(id+"F0.imprint","IMPRINT",EDGE,{"derivedFrom":subQ3}),1.0]])]});}
            var Q40;
            {var subQ3=sQuery(id+"F0.wireOp",EDGE,"2390580b-736b-4805-a3aa-b3ade61d923c.rect.top");Q40=makeQuery(id+"F0.imprint","IMPRINT",FACE,{"disambiguationData":[TD([[makeQuery(id+"F0.imprint","IMPRINT",EDGE,{"derivedFrom":subQ3}),-1.0]])]});}
            var Q41;
            {var subQ0=sQuery(id+"F0.wireOp",EDGE,"2166e6f4-a4c2-4c34-8466-9477065b0f98.rect.left");Q41=makeQuery(id+"F0.imprint","IMPRINT",FACE,{"disambiguationData":[TD([[makeQuery(id+"F0.imprint","IMPRINT",EDGE,{"derivedFrom":subQ0}),1.0]])]});}
            var Q42;
            {var subQ0=sQuery(id+"F0.wireOp",EDGE,"2166e6f4-a4c2-4c34-8466-9477065b0f98.rect.right");Q42=makeQuery(id+"F0.imprint","IMPRINT",FACE,{"disambiguationData":[TD([[makeQuery(id+"F0.imprint","IMPRINT",EDGE,{"derivedFrom":subQ0}),-1.0]])]});}
            var Q43;
            {var subQ3=sQuery(id+"F0.wireOp",EDGE,"a0b229e6-3aa1-4465-9a5a-0985d3e63f01.rect.top");Q43=makeQuery(id+"F0.imprint","IMPRINT",FACE,{"disambiguationData":[TD([[makeQuery(id+"F0.imprint","IMPRINT",EDGE,{"derivedFrom":subQ3}),-1.0]])]});}
            var Q44;
            {var subQ0=sQuery(id+"F0.wireOp",EDGE,"1c78e4fe-e1cb-4ebb-b1fd-c2c0064fb7eb.rect.right");Q44=makeQuery(id+"F0.imprint","IMPRINT",FACE,{"disambiguationData":[TD([[makeQuery(id+"F0.imprint","IMPRINT",EDGE,{"derivedFrom":subQ0}),-1.0]])]});}
            var Q45;
            {var subQ3=sQuery(id+"F0.wireOp",EDGE,"6cf41ee3-29a7-4b54-a486-07bb11f7813b.rect.top");Q45=makeQuery(id+"F0.imprint","IMPRINT",FACE,{"disambiguationData":[TD([[makeQuery(id+"F0.imprint","IMPRINT",EDGE,{"derivedFrom":subQ3}),-1.0]])]});}
            var Q46;
            {var subQ0=sQuery(id+"F0.wireOp",EDGE,"892f925b-46cd-4a3b-8f99-ca5bc6e0e537.rect.right");Q46=makeQuery(id+"F0.imprint","IMPRINT",FACE,{"disambiguationData":[TD([[makeQuery(id+"F0.imprint","IMPRINT",EDGE,{"derivedFrom":subQ0}),1.0]])]});}
            var Q47;
            {var subQ3=sQuery(id+"F0.wireOp",EDGE,"6cf41ee3-29a7-4b54-a486-07bb11f7813b.rect.bottom");Q47=makeQuery(id+"F0.imprint","IMPRINT",FACE,{"disambiguationData":[TD([[makeQuery(id+"F0.imprint","IMPRINT",EDGE,{"derivedFrom":subQ3}),1.0]])]});}
            var Q48;
            {var subQ0=sQuery(id+"F0.wireOp",EDGE,"892f925b-46cd-4a3b-8f99-ca5bc6e0e537.rect.left");Q48=makeQuery(id+"F0.imprint","IMPRINT",FACE,{"disambiguationData":[TD([[makeQuery(id+"F0.imprint","IMPRINT",EDGE,{"derivedFrom":subQ0}),-1.0]])]});}
            var Q49;
            {var subQ3=sQuery(id+"F0.wireOp",EDGE,"a0b229e6-3aa1-4465-9a5a-0985d3e63f01.rect.bottom");Q49=makeQuery(id+"F0.imprint","IMPRINT",FACE,{"disambiguationData":[TD([[makeQuery(id+"F0.imprint","IMPRINT",EDGE,{"derivedFrom":subQ3}),1.0]])]});}
            var Q50;
            {var subQ0=sQuery(id+"F0.wireOp",EDGE,"1c78e4fe-e1cb-4ebb-b1fd-c2c0064fb7eb.rect.left");Q50=makeQuery(id+"F0.imprint","IMPRINT",FACE,{"disambiguationData":[TD([[makeQuery(id+"F0.imprint","IMPRINT",EDGE,{"derivedFrom":subQ0}),1.0]])]});}
            var Q51;
            {var subQ3=sQuery(id+"F0.wireOp",EDGE,"f48832b2-2d0e-43cf-9fc1-d9ed1891b05c.rect.top");Q51=makeQuery(id+"F0.imprint","IMPRINT",FACE,{"disambiguationData":[TD([[makeQuery(id+"F0.imprint","IMPRINT",EDGE,{"derivedFrom":subQ3}),-1.0]])]});}
            var Q52;
            {var subQ3=sQuery(id+"F0.wireOp",EDGE,"f48832b2-2d0e-43cf-9fc1-d9ed1891b05c.rect.bottom");Q52=makeQuery(id+"F0.imprint","IMPRINT",FACE,{"disambiguationData":[TD([[makeQuery(id+"F0.imprint","IMPRINT",EDGE,{"derivedFrom":subQ3}),1.0]])]});}
            var Q53;
            {var subQ0=sQuery(id+"F0.wireOp",EDGE,"1b435d11-bbf8-4d76-92a6-f0dfc75fd8fa.rect.left");Q53=makeQuery(id+"F0.imprint","IMPRINT",FACE,{"disambiguationData":[TD([[makeQuery(id+"F0.imprint","IMPRINT",EDGE,{"derivedFrom":subQ0}),-1.0]])]});}
            var Q54;
            {var subQ0=sQuery(id+"F0.wireOp",EDGE,"1b435d11-bbf8-4d76-92a6-f0dfc75fd8fa.rect.right");Q54=makeQuery(id+"F0.imprint","IMPRINT",FACE,{"disambiguationData":[TD([[makeQuery(id+"F0.imprint","IMPRINT",EDGE,{"derivedFrom":subQ0}),1.0]])]});}
            var Q55;
            {var subQ3=sQuery(id+"F0.wireOp",EDGE,"e5a37d3b-96b8-4f85-b028-1329ce64cde0.rect.top");Q55=makeQuery(id+"F0.imprint","IMPRINT",FACE,{"disambiguationData":[TD([[makeQuery(id+"F0.imprint","IMPRINT",EDGE,{"derivedFrom":subQ3}),-1.0]])]});}
            var Q56;
            {var subQ3=sQuery(id+"F0.wireOp",EDGE,"e5a37d3b-96b8-4f85-b028-1329ce64cde0.rect.bottom");Q56=makeQuery(id+"F0.imprint","IMPRINT",FACE,{"disambiguationData":[TD([[makeQuery(id+"F0.imprint","IMPRINT",EDGE,{"derivedFrom":subQ3}),1.0]])]});}
            var Q57;
            {var subQ1=sQuery(id+"F0.wireOp",EDGE,"17f1270a-2747-4b10-848f-e92c6a9a448e.rect.bottom");Q57=makeQuery(id+"F0.imprint","IMPRINT",FACE,{"disambiguationData":[TD([[makeQuery(id+"F0.imprint","IMPRINT",EDGE,{"derivedFrom":subQ1}),-1.0]])]});}
            var Q58;
            {var subQ1=sQuery(id+"F0.wireOp",EDGE,"b581c809-2514-4fc4-bae3-9c6477576331.rect.bottom");Q58=makeQuery(id+"F0.imprint","IMPRINT",FACE,{"disambiguationData":[TD([[makeQuery(id+"F0.imprint","IMPRINT",EDGE,{"derivedFrom":subQ1}),-1.0]])]});}
            var Q59;
            Q59=makeQuery(id+"F0.imprint","IMPRINT",FACE,{"disambiguationData":[TD([[makeQuery(id+"F0.imprint","IMPRINT",EDGE,{"derivedFrom":sQuery(id+"F0.wireOp",EDGE,"575d105f-47f6-455c-9778-bb3c833a7581.rect.bottom")}),-1.0]])]});
            var Q60;
            {var subQ1=sQuery(id+"F0.wireOp",EDGE,"fff48876-04e1-4fc8-9402-123f03e55176.rect.bottom");Q60=makeQuery(id+"F0.imprint","IMPRINT",FACE,{"disambiguationData":[TD([[makeQuery(id+"F0.imprint","IMPRINT",EDGE,{"derivedFrom":subQ1}),1.0]])]});}
            var Q61;
            {var subQ1=sQuery(id+"F0.wireOp",EDGE,"13d43389-c631-4c73-802b-5182c9e3e657.rect.bottom");Q61=makeQuery(id+"F0.imprint","IMPRINT",FACE,{"disambiguationData":[TD([[makeQuery(id+"F0.imprint","IMPRINT",EDGE,{"derivedFrom":subQ1}),1.0]])]});}
            var Q62;
            Q62=makeQuery(id+"F0.imprint","IMPRINT",FACE,{"disambiguationData":[TD([[makeQuery(id+"F0.imprint","IMPRINT",EDGE,{"derivedFrom":sQuery(id+"F0.wireOp",EDGE,"7228705b-8608-42c8-9eaf-56973434d279.rect.bottom")}),1.0]])]});
            var Q63;
            {var subQ1=sQuery(id+"F0.wireOp",EDGE,"a5fb6563-f1c4-4e54-b2d2-c845c3ec7855.rect.bottom");Q63=makeQuery(id+"F0.imprint","IMPRINT",FACE,{"disambiguationData":[TD([[makeQuery(id+"F0.imprint","IMPRINT",EDGE,{"derivedFrom":subQ1}),-1.0]])]});}
            var Q64;
            {var subQ1=sQuery(id+"F0.wireOp",EDGE,"528f5d14-1237-4880-831d-745eabb57258.rect.bottom");Q64=makeQuery(id+"F0.imprint","IMPRINT",FACE,{"disambiguationData":[TD([[makeQuery(id+"F0.imprint","IMPRINT",EDGE,{"derivedFrom":subQ1}),-1.0]])]});}
            var Q65;
            {var subQ1=sQuery(id+"F0.wireOp",EDGE,"3a1d95bb-315e-45e8-9574-3d48fc663a87.rect.bottom");Q65=makeQuery(id+"F0.imprint","IMPRINT",FACE,{"disambiguationData":[TD([[makeQuery(id+"F0.imprint","IMPRINT",EDGE,{"derivedFrom":subQ1}),-1.0]])]});}
            var Q66;
            Q66=makeQuery(id+"F0.imprint","IMPRINT",FACE,{"disambiguationData":[TD([[makeQuery(id+"F0.imprint","IMPRINT",EDGE,{"derivedFrom":sQuery(id+"F0.wireOp",EDGE,"9606da7c-27d0-4a8d-8844-21ce520e0263.rect.bottom")}),1.0]])]});
            var Q67;
            {var subQ1=sQuery(id+"F0.wireOp",EDGE,"2a591dfd-ceba-4041-ab34-b8e9dd08917c.rect.bottom");Q67=makeQuery(id+"F0.imprint","IMPRINT",FACE,{"disambiguationData":[TD([[makeQuery(id+"F0.imprint","IMPRINT",EDGE,{"derivedFrom":subQ1}),-1.0]])]});}
            var Q68;
            {var subQ1=sQuery(id+"F0.wireOp",EDGE,"a0e47c1a-8269-4cee-a721-aee1dfa80837.rect.bottom");Q68=makeQuery(id+"F0.imprint","IMPRINT",FACE,{"disambiguationData":[TD([[makeQuery(id+"F0.imprint","IMPRINT",EDGE,{"derivedFrom":subQ1}),-1.0]])]});}
            var Q69;
            Q69=makeQuery(id+"F0.imprint","IMPRINT",FACE,{"disambiguationData":[TD([[makeQuery(id+"F0.imprint","IMPRINT",EDGE,{"derivedFrom":sQuery(id+"F0.wireOp",EDGE,"E35.rect.bottom")}),-1.0]])]});
            var Q70;
            Q70=makeQuery(id+"F0.imprint","IMPRINT",FACE,{"disambiguationData":[TD([[makeQuery(id+"F0.imprint","IMPRINT",EDGE,{"derivedFrom":sQuery(id+"F0.wireOp",EDGE,"E32.rect.top")}),-1.0]])]});
            var Q71;
            Q71=makeQuery(id+"F0.imprint","IMPRINT",FACE,{"disambiguationData":[TD([[makeQuery(id+"F0.imprint","IMPRINT",EDGE,{"derivedFrom":sQuery(id+"F0.wireOp",EDGE,"E32.rect.bottom")}),-1.0]])]});
            var Q72;
            Q72=makeQuery(id+"F0.imprint","IMPRINT",FACE,{"disambiguationData":[TD([[makeQuery(id+"F0.imprint","IMPRINT",EDGE,{"derivedFrom":sQuery(id+"F0.wireOp",EDGE,"E45")}),1.0]])]});
            var Q73;
            Q73=makeQuery(id+"F0.imprint","IMPRINT",FACE,{"disambiguationData":[TD([[makeQuery(id+"F0.imprint","IMPRINT",EDGE,{"derivedFrom":sQuery(id+"F0.wireOp",EDGE,"E46")}),1.0]])]});
            var Q74;
            Q74=makeQuery(id+"F0.imprint","IMPRINT",FACE,{"disambiguationData":[TD([[makeQuery(id+"F0.imprint","IMPRINT",EDGE,{"derivedFrom":sQuery(id+"F0.wireOp",EDGE,"E48")}),1.0]])]});
            var Q75;
            Q75=makeQuery(id+"F0.imprint","IMPRINT",FACE,{"disambiguationData":[TD([[makeQuery(id+"F0.imprint","IMPRINT",EDGE,{"derivedFrom":sQuery(id+"F0.wireOp",EDGE,"E47")}),1.0]])]});
            var Q76;
            Q76=makeQuery(id+"F0.imprint","IMPRINT",FACE,{"disambiguationData":[TD([[makeQuery(id+"F0.imprint","IMPRINT",EDGE,{"derivedFrom":sQuery(id+"F0.wireOp",EDGE,"E50")}),1.0]])]});
            var Q77;
            Q77=makeQuery(id+"F0.imprint","IMPRINT",FACE,{"disambiguationData":[TD([[makeQuery(id+"F0.imprint","IMPRINT",EDGE,{"derivedFrom":sQuery(id+"F0.wireOp",EDGE,"E49")}),1.0]])]});
            var Q78;
            Q78=makeQuery(id+"F0.imprint","IMPRINT",FACE,{"disambiguationData":[TD([[makeQuery(id+"F0.imprint","IMPRINT",EDGE,{"derivedFrom":sQuery(id+"F0.wireOp",EDGE,"E33")}),1.0]])]});
            var Q79;
            Q79=makeQuery(id+"F0.imprint","IMPRINT",FACE,{"disambiguationData":[TD([[makeQuery(id+"F0.imprint","IMPRINT",EDGE,{"derivedFrom":sQuery(id+"F0.wireOp",EDGE,"E56.rect.bottom")}),1.0]])]});
            var Q80;
            {var subQ1=sQuery(id+"F0.wireOp",EDGE,"E57.rect.bottom");Q80=makeQuery(id+"F0.imprint","IMPRINT",FACE,{"disambiguationData":[TD([[makeQuery(id+"F0.imprint","IMPRINT",EDGE,{"derivedFrom":subQ1}),1.0]])]});}
            var Q81;
            {var subQ1=sQuery(id+"F0.wireOp",EDGE,"E59.rect.bottom");Q81=makeQuery(id+"F0.imprint","IMPRINT",FACE,{"disambiguationData":[TD([[makeQuery(id+"F0.imprint","IMPRINT",EDGE,{"derivedFrom":subQ1}),1.0]])]});}
            var Q82;
            {var subQ1=sQuery(id+"F0.wireOp",EDGE,"E55.rect.bottom");Q82=makeQuery(id+"F0.imprint","IMPRINT",FACE,{"disambiguationData":[TD([[makeQuery(id+"F0.imprint","IMPRINT",EDGE,{"derivedFrom":subQ1}),1.0]])]});}
            var Q83;
            Q83=makeQuery(id+"F0.imprint","IMPRINT",FACE,{"disambiguationData":[TD([[makeQuery(id+"F0.imprint","IMPRINT",EDGE,{"derivedFrom":sQuery(id+"F0.wireOp",EDGE,"E54.rect.bottom")}),-1.0]])]});
            var Q84;
            {var subQ0=sQuery(id+"F0.wireOp",EDGE,"E51.rect.bottom");Q84=makeQuery(id+"F0.imprint","IMPRINT",FACE,{"disambiguationData":[TD([[makeQuery(id+"F0.imprint","IMPRINT",EDGE,{"derivedFrom":subQ0}),-1.0]])]});}
            var Q85;
            {var subQ1=sQuery(id+"F0.wireOp",EDGE,"E52.rect.bottom");Q85=makeQuery(id+"F0.imprint","IMPRINT",FACE,{"disambiguationData":[TD([[makeQuery(id+"F0.imprint","IMPRINT",EDGE,{"derivedFrom":subQ1}),1.0]])]});}
            var Q86;
            {var subQ0=sQuery(id+"F0.wireOp",EDGE,"E62.rect.bottom");Q86=makeQuery(id+"F0.imprint","IMPRINT",FACE,{"disambiguationData":[TD([[makeQuery(id+"F0.imprint","IMPRINT",EDGE,{"derivedFrom":subQ0}),-1.0]])]});}
            var Q87;
            Q87=makeQuery(id+"F0.imprint","IMPRINT",FACE,{"disambiguationData":[TD([[makeQuery(id+"F0.imprint","IMPRINT",EDGE,{"derivedFrom":sQuery(id+"F0.wireOp",EDGE,"E53.rect.bottom")}),1.0]])]});
            var Q88;
            Q88=makeQuery(id+"F0.imprint","IMPRINT",FACE,{"disambiguationData":[TD([[makeQuery(id+"F0.imprint","IMPRINT",EDGE,{"derivedFrom":sQuery(id+"F0.wireOp",EDGE,"E64.rect.bottom")}),1.0]])]});
            var Q89;
            {var subQ1=sQuery(id+"F0.wireOp",EDGE,"E63.rect.bottom");Q89=makeQuery(id+"F0.imprint","IMPRINT",FACE,{"disambiguationData":[TD([[makeQuery(id+"F0.imprint","IMPRINT",EDGE,{"derivedFrom":subQ1}),1.0]])]});}
            var Q90;
            {var subQ1=sQuery(id+"F0.wireOp",EDGE,"E69.rect.bottom");Q90=makeQuery(id+"F0.imprint","IMPRINT",FACE,{"disambiguationData":[TD([[makeQuery(id+"F0.imprint","IMPRINT",EDGE,{"derivedFrom":subQ1}),1.0]])]});}
            var Q91;
            Q91=makeQuery(id+"F0.imprint","IMPRINT",FACE,{"disambiguationData":[TD([[makeQuery(id+"F0.imprint","IMPRINT",EDGE,{"derivedFrom":sQuery(id+"F0.wireOp",EDGE,"E58.rect.bottom")}),1.0]])]});
            var Q92;
            Q92=makeQuery(id+"F0.imprint","IMPRINT",FACE,{"disambiguationData":[TD([[makeQuery(id+"F0.imprint","IMPRINT",EDGE,{"derivedFrom":sQuery(id+"F0.wireOp",EDGE,"E61.rect.bottom")}),-1.0]])]});
            var Q93;
            {var subQ1=sQuery(id+"F0.wireOp",EDGE,"E60.rect.bottom");Q93=makeQuery(id+"F0.imprint","IMPRINT",FACE,{"disambiguationData":[TD([[makeQuery(id+"F0.imprint","IMPRINT",EDGE,{"derivedFrom":subQ1}),1.0]])]});}
            var Q94;
            {var subQ1=sQuery(id+"F0.wireOp",EDGE,"E70.rect.bottom");Q94=makeQuery(id+"F0.imprint","IMPRINT",FACE,{"disambiguationData":[TD([[makeQuery(id+"F0.imprint","IMPRINT",EDGE,{"derivedFrom":subQ1}),1.0]])]});}
            var Q95;
            {var subQ1=sQuery(id+"F0.wireOp",EDGE,"E73.rect.bottom");Q95=makeQuery(id+"F0.imprint","IMPRINT",FACE,{"disambiguationData":[TD([[makeQuery(id+"F0.imprint","IMPRINT",EDGE,{"derivedFrom":subQ1}),-1.0]])]});}
            var Q96;
            Q96=makeQuery(id+"F0.imprint","IMPRINT",FACE,{"disambiguationData":[TD([[makeQuery(id+"F0.imprint","IMPRINT",EDGE,{"derivedFrom":sQuery(id+"F0.wireOp",EDGE,"E65.rect.bottom")}),-1.0]])]});
            var Q97;
            {var subQ1=sQuery(id+"F0.wireOp",EDGE,"E66.rect.bottom");Q97=makeQuery(id+"F0.imprint","IMPRINT",FACE,{"disambiguationData":[TD([[makeQuery(id+"F0.imprint","IMPRINT",EDGE,{"derivedFrom":subQ1}),1.0]])]});}
            var Q98;
            {var subQ0=sQuery(id+"F0.wireOp",EDGE,"E67.rect.bottom");Q98=makeQuery(id+"F0.imprint","IMPRINT",FACE,{"disambiguationData":[TD([[makeQuery(id+"F0.imprint","IMPRINT",EDGE,{"derivedFrom":subQ0}),1.0]])]});}
            var Q99;
            {var subQ1=sQuery(id+"F0.wireOp",EDGE,"E72.rect.bottom");Q99=makeQuery(id+"F0.imprint","IMPRINT",FACE,{"disambiguationData":[TD([[makeQuery(id+"F0.imprint","IMPRINT",EDGE,{"derivedFrom":subQ1}),-1.0]])]});}
            var Q100;
            Q100=makeQuery(id+"F0.imprint","IMPRINT",FACE,{"disambiguationData":[TD([[makeQuery(id+"F0.imprint","IMPRINT",EDGE,{"derivedFrom":sQuery(id+"F0.wireOp",EDGE,"E68.rect.bottom")}),1.0]])]});
            var Q101;
            Q101=makeQuery(id+"F0.imprint","IMPRINT",FACE,{"disambiguationData":[TD([[makeQuery(id+"F0.imprint","IMPRINT",EDGE,{"derivedFrom":sQuery(id+"F0.wireOp",EDGE,"E71.rect.bottom")}),1.0]])]});
            extrude(context, id + "F1", {"entities" : qUnion([Q0, Q1, Q2, Q3, Q4, Q5, Q6, Q7, Q8, Q9, Q10, Q11, Q12, Q13, Q14, Q15, Q16, Q17, Q18, Q19, Q20, Q21, Q22, Q23, Q24, Q25, Q26, Q27, Q28, Q29, Q30, Q31, Q32, Q33, Q34, Q35, Q36, Q37, Q38, Q39, Q40, Q41, Q42, Q43, Q44, Q45, Q46, Q47, Q48, Q49, Q50, Q51, Q52, Q53, Q54, Q55, Q56, Q57, Q58, Q59, Q60, Q61, Q62, Q63, Q64, Q65, Q66, Q67, Q68, Q69, Q70, Q71, Q72, Q73, Q74, Q75, Q76, Q77, Q78, Q79, Q80, Q81, Q82, Q83, Q84, Q85, Q86, Q87, Q88, Q89, Q90, Q91, Q92, Q93, Q94, Q95, Q96, Q97, Q98, Q99, Q100, Q101]), "oppositeDirection" : true, "depth" : 4 * mm});
        }
        {
            var Q0;
            {var subQ1=sQuery(id+"F0.wireOp",EDGE,"839c260c-2e27-47bf-a2f2-8bfdeadb8496.2");var subQ3=sQuery(id+"F0.wireOp",EDGE,"839c260c-2e27-47bf-a2f2-8bfdeadb8496.1");var subQ5=makeQuery(id+"F0.imprint","INTERSECT",VERTEX,{"derivedFrom":[subQ3,subQ1]});Q0=makeQuery(id+"F0.imprint","IMPRINT",FACE,{"disambiguationData":[TD([[makeQuery(id+"F0.imprint","IMPRINT",EDGE,{"disambiguationData":[TD([[subQ5,1.0]])],"derivedFrom":subQ3}),-1.0]])]});}
            var Q1;
            {var subQ1=sQuery(id+"F0.wireOp",EDGE,"839c260c-2e27-47bf-a2f2-8bfdeadb8496.2");var subQ3=sQuery(id+"F0.wireOp",EDGE,"839c260c-2e27-47bf-a2f2-8bfdeadb8496.1");var subQ5=makeQuery(id+"F0.imprint","INTERSECT",VERTEX,{"derivedFrom":[subQ3,subQ1]});Q1=makeQuery(id+"F0.imprint","IMPRINT",FACE,{"disambiguationData":[TD([[makeQuery(id+"F0.imprint","IMPRINT",EDGE,{"disambiguationData":[TD([[subQ5,1.0]])],"derivedFrom":subQ3}),1.0]])]});}
            var Q2;
            {var subQ1=sQuery(id+"F0.wireOp",EDGE,"839c260c-2e27-47bf-a2f2-8bfdeadb8496.3");var subQ3=sQuery(id+"F0.wireOp",EDGE,"839c260c-2e27-47bf-a2f2-8bfdeadb8496.2");var subQ5=makeQuery(id+"F0.imprint","INTERSECT",VERTEX,{"derivedFrom":[subQ3,subQ1]});Q2=makeQuery(id+"F0.imprint","IMPRINT",FACE,{"disambiguationData":[TD([[makeQuery(id+"F0.imprint","IMPRINT",EDGE,{"disambiguationData":[TD([[subQ5,1.0]])],"derivedFrom":subQ3}),1.0]])]});}
            var Q3;
            {var subQ1=sQuery(id+"F0.wireOp",EDGE,"839c260c-2e27-47bf-a2f2-8bfdeadb8496.3");var subQ3=sQuery(id+"F0.wireOp",EDGE,"839c260c-2e27-47bf-a2f2-8bfdeadb8496.2");var subQ5=makeQuery(id+"F0.imprint","INTERSECT",VERTEX,{"derivedFrom":[subQ3,subQ1]});Q3=makeQuery(id+"F0.imprint","IMPRINT",FACE,{"disambiguationData":[TD([[makeQuery(id+"F0.imprint","IMPRINT",EDGE,{"disambiguationData":[TD([[subQ5,1.0]])],"derivedFrom":subQ3}),-1.0]])]});}
            var Q4;
            {var subQ1=sQuery(id+"F0.wireOp",EDGE,"839c260c-2e27-47bf-a2f2-8bfdeadb8496.3");var subQ3=sQuery(id+"F0.wireOp",EDGE,"839c260c-2e27-47bf-a2f2-8bfdeadb8496.0");var subQ5=makeQuery(id+"F0.imprint","INTERSECT",VERTEX,{"derivedFrom":[subQ3,subQ1]});Q4=makeQuery(id+"F0.imprint","IMPRINT",FACE,{"disambiguationData":[TD([[makeQuery(id+"F0.imprint","IMPRINT",EDGE,{"disambiguationData":[TD([[subQ5,1.0]])],"derivedFrom":subQ3}),-1.0]])]});}
            var Q5;
            {var subQ1=sQuery(id+"F0.wireOp",EDGE,"839c260c-2e27-47bf-a2f2-8bfdeadb8496.3");var subQ3=sQuery(id+"F0.wireOp",EDGE,"839c260c-2e27-47bf-a2f2-8bfdeadb8496.0");var subQ5=makeQuery(id+"F0.imprint","INTERSECT",VERTEX,{"derivedFrom":[subQ3,subQ1]});Q5=makeQuery(id+"F0.imprint","IMPRINT",FACE,{"disambiguationData":[TD([[makeQuery(id+"F0.imprint","IMPRINT",EDGE,{"disambiguationData":[TD([[subQ5,1.0]])],"derivedFrom":subQ3}),1.0]])]});}
            var Q6;
            {var subQ0=sQuery(id+"F0.wireOp",EDGE,"E24");var subQ3=sQuery(id+"F0.wireOp",EDGE,"839c260c-2e27-47bf-a2f2-8bfdeadb8496.0");var subQ4=makeQuery(id+"F0.imprint","INTERSECT",VERTEX,{"derivedFrom":[subQ3,subQ0]});Q6=makeQuery(id+"F0.imprint","IMPRINT",FACE,{"disambiguationData":[TD([[makeQuery(id+"F0.imprint","IMPRINT",EDGE,{"disambiguationData":[TD([[subQ4,-1.0]])],"derivedFrom":subQ3}),-1.0]])]});}
            var Q7;
            {var subQ0=sQuery(id+"F0.wireOp",EDGE,"E24");var subQ3=sQuery(id+"F0.wireOp",EDGE,"839c260c-2e27-47bf-a2f2-8bfdeadb8496.0");var subQ4=makeQuery(id+"F0.imprint","INTERSECT",VERTEX,{"derivedFrom":[subQ3,subQ0]});Q7=makeQuery(id+"F0.imprint","IMPRINT",FACE,{"disambiguationData":[TD([[makeQuery(id+"F0.imprint","IMPRINT",EDGE,{"disambiguationData":[TD([[subQ4,-1.0]])],"derivedFrom":subQ3}),1.0]])]});}
            var Q8;
            Q8=makeQuery(id+"F0.imprint","IMPRINT",FACE,{"disambiguationData":[TD([[makeQuery(id+"F0.imprint","IMPRINT",EDGE,{"derivedFrom":sQuery(id+"F0.wireOp",EDGE,"E0.bottom")}),-1.0]])]});
            extrude(context, id + "F2", {"entities" : qUnion([Q0, Q1, Q2, Q3, Q4, Q5, Q6, Q7, Q8]), "operationType" : NewBodyOperationType.ADD, "depth" : 4 * mm});
        }
        {
            var Q0;
            Q0=makeQuery(id+"F0.imprint","IMPRINT",FACE,{"disambiguationData":[TD([[makeQuery(id+"F0.imprint","IMPRINT",EDGE,{"derivedFrom":sQuery(id+"F0.wireOp",EDGE,"E13.bottom")}),-1.0]])]});
            var Q1;
            Q1=makeQuery(id+"F0.imprint","IMPRINT",FACE,{"disambiguationData":[TD([[makeQuery(id+"F0.imprint","IMPRINT",EDGE,{"derivedFrom":sQuery(id+"F0.wireOp",EDGE,"E7.left")}),1.0]])]});
            var Q2;
            Q2=makeQuery(id+"F0.imprint","IMPRINT",FACE,{"disambiguationData":[TD([[makeQuery(id+"F0.imprint","IMPRINT",EDGE,{"derivedFrom":sQuery(id+"F0.wireOp",EDGE,"E14.right")}),1.0]])]});
            var Q3;
            Q3=makeQuery(id+"F0.imprint","IMPRINT",FACE,{"disambiguationData":[TD([[makeQuery(id+"F0.imprint","IMPRINT",EDGE,{"derivedFrom":sQuery(id+"F0.wireOp",EDGE,"E15.rect.bottom")}),1.0]])]});
            var Q4;
            Q4=makeQuery(id+"F0.imprint","IMPRINT",FACE,{"disambiguationData":[TD([[makeQuery(id+"F0.imprint","IMPRINT",EDGE,{"derivedFrom":sQuery(id+"F0.wireOp",EDGE,"E8.bottom")}),-1.0]])]});
            var Q5;
            Q5=makeQuery(id+"F0.imprint","IMPRINT",FACE,{"disambiguationData":[TD([[makeQuery(id+"F0.imprint","IMPRINT",EDGE,{"derivedFrom":sQuery(id+"F0.wireOp",EDGE,"E6.top")}),-1.0]])]});
            var Q6;
            Q6=makeQuery(id+"F0.imprint","IMPRINT",FACE,{"disambiguationData":[TD([[makeQuery(id+"F0.imprint","IMPRINT",EDGE,{"derivedFrom":sQuery(id+"F0.wireOp",EDGE,"E11.bottom")}),1.0]])]});
            var Q7;
            Q7=makeQuery(id+"F0.imprint","IMPRINT",FACE,{"disambiguationData":[TD([[makeQuery(id+"F0.imprint","IMPRINT",EDGE,{"derivedFrom":sQuery(id+"F0.wireOp",EDGE,"E17.1.0.34")}),1.0]])]});
            var Q8;
            Q8=makeQuery(id+"F0.imprint","IMPRINT",FACE,{"disambiguationData":[TD([[makeQuery(id+"F0.imprint","IMPRINT",EDGE,{"derivedFrom":sQuery(id+"F0.wireOp",EDGE,"E17.1.0.35")}),-1.0]])]});
            var Q9;
            Q9=makeQuery(id+"F0.imprint","IMPRINT",FACE,{"disambiguationData":[TD([[makeQuery(id+"F0.imprint","IMPRINT",EDGE,{"derivedFrom":sQuery(id+"F0.wireOp",EDGE,"E17.1.0.12")}),-1.0]])]});
            var Q10;
            Q10=makeQuery(id+"F0.imprint","IMPRINT",FACE,{"disambiguationData":[TD([[makeQuery(id+"F0.imprint","IMPRINT",EDGE,{"derivedFrom":sQuery(id+"F0.wireOp",EDGE,"E17.1.0.38")}),1.0]])]});
            var Q11;
            Q11=makeQuery(id+"F0.imprint","IMPRINT",FACE,{"disambiguationData":[TD([[makeQuery(id+"F0.imprint","IMPRINT",EDGE,{"derivedFrom":sQuery(id+"F0.wireOp",EDGE,"E17.1.0.15")}),-1.0]])]});
            var Q12;
            Q12=makeQuery(id+"F0.imprint","IMPRINT",FACE,{"disambiguationData":[TD([[makeQuery(id+"F0.imprint","IMPRINT",EDGE,{"derivedFrom":sQuery(id+"F0.wireOp",EDGE,"E17.1.0.5")}),1.0]])]});
            var Q13;
            Q13=makeQuery(id+"F0.imprint","IMPRINT",FACE,{"disambiguationData":[TD([[makeQuery(id+"F0.imprint","IMPRINT",EDGE,{"derivedFrom":sQuery(id+"F0.wireOp",EDGE,"E17.1.0.7")}),-1.0]])]});
            var Q14;
            Q14=makeQuery(id+"F0.imprint","IMPRINT",FACE,{"disambiguationData":[TD([[makeQuery(id+"F0.imprint","IMPRINT",EDGE,{"derivedFrom":sQuery(id+"F0.wireOp",EDGE,"E17.2.0.15")}),-1.0]])]});
            var Q15;
            Q15=makeQuery(id+"F0.imprint","IMPRINT",FACE,{"disambiguationData":[TD([[makeQuery(id+"F0.imprint","IMPRINT",EDGE,{"derivedFrom":sQuery(id+"F0.wireOp",EDGE,"E17.2.0.5")}),1.0]])]});
            var Q16;
            Q16=makeQuery(id+"F0.imprint","IMPRINT",FACE,{"disambiguationData":[TD([[makeQuery(id+"F0.imprint","IMPRINT",EDGE,{"derivedFrom":sQuery(id+"F0.wireOp",EDGE,"E17.2.0.7")}),-1.0]])]});
            var Q17;
            Q17=makeQuery(id+"F0.imprint","IMPRINT",FACE,{"disambiguationData":[TD([[makeQuery(id+"F0.imprint","IMPRINT",EDGE,{"derivedFrom":sQuery(id+"F0.wireOp",EDGE,"E17.2.0.38")}),1.0]])]});
            var Q18;
            Q18=makeQuery(id+"F0.imprint","IMPRINT",FACE,{"disambiguationData":[TD([[makeQuery(id+"F0.imprint","IMPRINT",EDGE,{"derivedFrom":sQuery(id+"F0.wireOp",EDGE,"E17.2.0.12")}),-1.0]])]});
            var Q19;
            Q19=makeQuery(id+"F0.imprint","IMPRINT",FACE,{"disambiguationData":[TD([[makeQuery(id+"F0.imprint","IMPRINT",EDGE,{"derivedFrom":sQuery(id+"F0.wireOp",EDGE,"E17.2.0.34")}),1.0]])]});
            var Q20;
            Q20=makeQuery(id+"F0.imprint","IMPRINT",FACE,{"disambiguationData":[TD([[makeQuery(id+"F0.imprint","IMPRINT",EDGE,{"derivedFrom":sQuery(id+"F0.wireOp",EDGE,"E17.2.0.35")}),-1.0]])]});
            var Q21;
            Q21=makeQuery(id+"F0.imprint","IMPRINT",FACE,{"disambiguationData":[TD([[makeQuery(id+"F0.imprint","IMPRINT",EDGE,{"derivedFrom":sQuery(id+"F0.wireOp",EDGE,"E17.3.0.35")}),-1.0]])]});
            var Q22;
            Q22=makeQuery(id+"F0.imprint","IMPRINT",FACE,{"disambiguationData":[TD([[makeQuery(id+"F0.imprint","IMPRINT",EDGE,{"derivedFrom":sQuery(id+"F0.wireOp",EDGE,"E17.3.0.34")}),1.0]])]});
            var Q23;
            Q23=makeQuery(id+"F0.imprint","IMPRINT",FACE,{"disambiguationData":[TD([[makeQuery(id+"F0.imprint","IMPRINT",EDGE,{"derivedFrom":sQuery(id+"F0.wireOp",EDGE,"E17.3.0.12")}),-1.0]])]});
            var Q24;
            Q24=makeQuery(id+"F0.imprint","IMPRINT",FACE,{"disambiguationData":[TD([[makeQuery(id+"F0.imprint","IMPRINT",EDGE,{"derivedFrom":sQuery(id+"F0.wireOp",EDGE,"E17.3.0.38")}),1.0]])]});
            var Q25;
            Q25=makeQuery(id+"F0.imprint","IMPRINT",FACE,{"disambiguationData":[TD([[makeQuery(id+"F0.imprint","IMPRINT",EDGE,{"derivedFrom":sQuery(id+"F0.wireOp",EDGE,"E17.3.0.15")}),-1.0]])]});
            var Q26;
            Q26=makeQuery(id+"F0.imprint","IMPRINT",FACE,{"disambiguationData":[TD([[makeQuery(id+"F0.imprint","IMPRINT",EDGE,{"derivedFrom":sQuery(id+"F0.wireOp",EDGE,"E17.3.0.7")}),-1.0]])]});
            var Q27;
            Q27=makeQuery(id+"F0.imprint","IMPRINT",FACE,{"disambiguationData":[TD([[makeQuery(id+"F0.imprint","IMPRINT",EDGE,{"derivedFrom":sQuery(id+"F0.wireOp",EDGE,"E17.3.0.5")}),1.0]])]});
            var Q28;
            Q28=makeQuery(id+"F0.imprint","IMPRINT",FACE,{"disambiguationData":[TD([[makeQuery(id+"F0.imprint","IMPRINT",EDGE,{"derivedFrom":sQuery(id+"F0.wireOp",EDGE,"E23")}),1.0]])]});
            var Q29;
            Q29=makeQuery(id+"F0.imprint","IMPRINT",FACE,{"disambiguationData":[TD([[makeQuery(id+"F0.imprint","IMPRINT",EDGE,{"derivedFrom":sQuery(id+"F0.wireOp",EDGE,"E22")}),1.0]])]});
            var Q30;
            Q30=makeQuery(id+"F0.imprint","IMPRINT",FACE,{"disambiguationData":[TD([[makeQuery(id+"F0.imprint","IMPRINT",EDGE,{"derivedFrom":sQuery(id+"F0.wireOp",EDGE,"E18.1.0.36")}),1.0]])]});
            var Q31;
            Q31=makeQuery(id+"F0.imprint","IMPRINT",FACE,{"disambiguationData":[TD([[makeQuery(id+"F0.imprint","IMPRINT",EDGE,{"derivedFrom":sQuery(id+"F0.wireOp",EDGE,"E18.1.0.61")}),1.0]])]});
            var Q32;
            Q32=makeQuery(id+"F0.imprint","IMPRINT",FACE,{"disambiguationData":[TD([[makeQuery(id+"F0.imprint","IMPRINT",EDGE,{"derivedFrom":sQuery(id+"F0.wireOp",EDGE,"E18.1.0.38")}),1.0]])]});
            var Q33;
            Q33=makeQuery(id+"F0.imprint","IMPRINT",FACE,{"disambiguationData":[TD([[makeQuery(id+"F0.imprint","IMPRINT",EDGE,{"derivedFrom":sQuery(id+"F0.wireOp",EDGE,"E18.1.0.53")}),-1.0]])]});
            var Q34;
            Q34=makeQuery(id+"F0.imprint","IMPRINT",FACE,{"disambiguationData":[TD([[makeQuery(id+"F0.imprint","IMPRINT",EDGE,{"derivedFrom":sQuery(id+"F0.wireOp",EDGE,"E18.1.0.54")}),1.0]])]});
            var Q35;
            Q35=makeQuery(id+"F0.imprint","IMPRINT",FACE,{"disambiguationData":[TD([[makeQuery(id+"F0.imprint","IMPRINT",EDGE,{"derivedFrom":sQuery(id+"F0.wireOp",EDGE,"E19.1.0.53")}),-1.0]])]});
            var Q36;
            Q36=makeQuery(id+"F0.imprint","IMPRINT",FACE,{"disambiguationData":[TD([[makeQuery(id+"F0.imprint","IMPRINT",EDGE,{"derivedFrom":sQuery(id+"F0.wireOp",EDGE,"E19.1.0.51")}),1.0]])]});
            var Q37;
            Q37=makeQuery(id+"F0.imprint","IMPRINT",FACE,{"disambiguationData":[TD([[makeQuery(id+"F0.imprint","IMPRINT",EDGE,{"derivedFrom":sQuery(id+"F0.wireOp",EDGE,"E18.1.0.51")}),1.0]])]});
            var Q38;
            Q38=makeQuery(id+"F0.imprint","IMPRINT",FACE,{"disambiguationData":[TD([[makeQuery(id+"F0.imprint","IMPRINT",EDGE,{"derivedFrom":sQuery(id+"F0.wireOp",EDGE,"E18.1.0.5")}),1.0]])]});
            var Q39;
            {var subQ1=sQuery(id+"F0.wireOp",EDGE,"a5fb6563-f1c4-4e54-b2d2-c845c3ec7855.rect.bottom");Q39=makeQuery(id+"F0.imprint","IMPRINT",FACE,{"disambiguationData":[TD([[makeQuery(id+"F0.imprint","IMPRINT",EDGE,{"derivedFrom":subQ1}),-1.0]])]});}
            var Q40;
            Q40=makeQuery(id+"F0.imprint","IMPRINT",FACE,{"disambiguationData":[TD([[makeQuery(id+"F0.imprint","IMPRINT",EDGE,{"derivedFrom":sQuery(id+"F0.wireOp",EDGE,"E33")}),1.0]])]});
            extrude(context, id + "F3", {"entities" : qUnion([Q0, Q1, Q2, Q3, Q4, Q5, Q6, Q7, Q8, Q9, Q10, Q11, Q12, Q13, Q14, Q15, Q16, Q17, Q18, Q19, Q20, Q21, Q22, Q23, Q24, Q25, Q26, Q27, Q28, Q29, Q30, Q31, Q32, Q33, Q34, Q35, Q36, Q37, Q38, Q39, Q40]), "operationType" : NewBodyOperationType.REMOVE, "oppositeDirection" : true, "offsetDistance" : 25 * mm, "depth" : 4 * mm});
        }
        {
            var Q0;
            Q0=makeQuery(id+"F0.imprint","IMPRINT",FACE,{"disambiguationData":[TD([[makeQuery(id+"F0.imprint","IMPRINT",EDGE,{"derivedFrom":sQuery(id+"F0.wireOp",EDGE,"E58.rect.bottom")}),1.0]])]});
            var Q1;
            {var subQ1=sQuery(id+"F0.wireOp",EDGE,"E60.rect.bottom");Q1=makeQuery(id+"F0.imprint","IMPRINT",FACE,{"disambiguationData":[TD([[makeQuery(id+"F0.imprint","IMPRINT",EDGE,{"derivedFrom":subQ1}),1.0]])]});}
            var Q2;
            {var subQ1=sQuery(id+"F0.wireOp",EDGE,"E59.rect.bottom");Q2=makeQuery(id+"F0.imprint","IMPRINT",FACE,{"disambiguationData":[TD([[makeQuery(id+"F0.imprint","IMPRINT",EDGE,{"derivedFrom":subQ1}),1.0]])]});}
            var Q3;
            {var subQ1=sQuery(id+"F0.wireOp",EDGE,"E66.rect.bottom");Q3=makeQuery(id+"F0.imprint","IMPRINT",FACE,{"disambiguationData":[TD([[makeQuery(id+"F0.imprint","IMPRINT",EDGE,{"derivedFrom":subQ1}),1.0]])]});}
            var Q4;
            Q4=makeQuery(id+"F0.imprint","IMPRINT",FACE,{"disambiguationData":[TD([[makeQuery(id+"F0.imprint","IMPRINT",EDGE,{"derivedFrom":sQuery(id+"F0.wireOp",EDGE,"E65.rect.bottom")}),-1.0]])]});
            var Q5;
            {var subQ0=sQuery(id+"F0.wireOp",EDGE,"E67.rect.bottom");Q5=makeQuery(id+"F0.imprint","IMPRINT",FACE,{"disambiguationData":[TD([[makeQuery(id+"F0.imprint","IMPRINT",EDGE,{"derivedFrom":subQ0}),1.0]])]});}
            var Q6;
            {var subQ1=sQuery(id+"F0.wireOp",EDGE,"E72.rect.bottom");Q6=makeQuery(id+"F0.imprint","IMPRINT",FACE,{"disambiguationData":[TD([[makeQuery(id+"F0.imprint","IMPRINT",EDGE,{"derivedFrom":subQ1}),-1.0]])]});}
            var Q7;
            {var subQ1=sQuery(id+"F0.wireOp",EDGE,"E73.rect.bottom");Q7=makeQuery(id+"F0.imprint","IMPRINT",FACE,{"disambiguationData":[TD([[makeQuery(id+"F0.imprint","IMPRINT",EDGE,{"derivedFrom":subQ1}),-1.0]])]});}
            var Q8;
            {var subQ1=sQuery(id+"F0.wireOp",EDGE,"E70.rect.bottom");Q8=makeQuery(id+"F0.imprint","IMPRINT",FACE,{"disambiguationData":[TD([[makeQuery(id+"F0.imprint","IMPRINT",EDGE,{"derivedFrom":subQ1}),1.0]])]});}
            var Q9;
            Q9=makeQuery(id+"F0.imprint","IMPRINT",FACE,{"disambiguationData":[TD([[makeQuery(id+"F0.imprint","IMPRINT",EDGE,{"derivedFrom":sQuery(id+"F0.wireOp",EDGE,"E68.rect.bottom")}),1.0]])]});
            var Q10;
            {var subQ1=sQuery(id+"F0.wireOp",EDGE,"E69.rect.bottom");Q10=makeQuery(id+"F0.imprint","IMPRINT",FACE,{"disambiguationData":[TD([[makeQuery(id+"F0.imprint","IMPRINT",EDGE,{"derivedFrom":subQ1}),1.0]])]});}
            var Q11;
            Q11=makeQuery(id+"F0.imprint","IMPRINT",FACE,{"disambiguationData":[TD([[makeQuery(id+"F0.imprint","IMPRINT",EDGE,{"derivedFrom":sQuery(id+"F0.wireOp",EDGE,"E71.rect.bottom")}),1.0]])]});
            var Q12;
            {var subQ1=sQuery(id+"F0.wireOp",EDGE,"E63.rect.bottom");Q12=makeQuery(id+"F0.imprint","IMPRINT",FACE,{"disambiguationData":[TD([[makeQuery(id+"F0.imprint","IMPRINT",EDGE,{"derivedFrom":subQ1}),1.0]])]});}
            var Q13;
            Q13=makeQuery(id+"F0.imprint","IMPRINT",FACE,{"disambiguationData":[TD([[makeQuery(id+"F0.imprint","IMPRINT",EDGE,{"derivedFrom":sQuery(id+"F0.wireOp",EDGE,"E64.rect.bottom")}),1.0]])]});
            var Q14;
            {var subQ0=sQuery(id+"F0.wireOp",EDGE,"E62.rect.bottom");Q14=makeQuery(id+"F0.imprint","IMPRINT",FACE,{"disambiguationData":[TD([[makeQuery(id+"F0.imprint","IMPRINT",EDGE,{"derivedFrom":subQ0}),-1.0]])]});}
            var Q15;
            Q15=makeQuery(id+"F0.imprint","IMPRINT",FACE,{"disambiguationData":[TD([[makeQuery(id+"F0.imprint","IMPRINT",EDGE,{"derivedFrom":sQuery(id+"F0.wireOp",EDGE,"E61.rect.bottom")}),-1.0]])]});
            var Q16;
            {var subQ1=sQuery(id+"F0.wireOp",EDGE,"E55.rect.bottom");Q16=makeQuery(id+"F0.imprint","IMPRINT",FACE,{"disambiguationData":[TD([[makeQuery(id+"F0.imprint","IMPRINT",EDGE,{"derivedFrom":subQ1}),1.0]])]});}
            var Q17;
            Q17=makeQuery(id+"F0.imprint","IMPRINT",FACE,{"disambiguationData":[TD([[makeQuery(id+"F0.imprint","IMPRINT",EDGE,{"derivedFrom":sQuery(id+"F0.wireOp",EDGE,"E56.rect.bottom")}),1.0]])]});
            var Q18;
            {var subQ1=sQuery(id+"F0.wireOp",EDGE,"E57.rect.bottom");Q18=makeQuery(id+"F0.imprint","IMPRINT",FACE,{"disambiguationData":[TD([[makeQuery(id+"F0.imprint","IMPRINT",EDGE,{"derivedFrom":subQ1}),1.0]])]});}
            var Q19;
            {var subQ1=sQuery(id+"F0.wireOp",EDGE,"E52.rect.bottom");Q19=makeQuery(id+"F0.imprint","IMPRINT",FACE,{"disambiguationData":[TD([[makeQuery(id+"F0.imprint","IMPRINT",EDGE,{"derivedFrom":subQ1}),1.0]])]});}
            var Q20;
            Q20=makeQuery(id+"F0.imprint","IMPRINT",FACE,{"disambiguationData":[TD([[makeQuery(id+"F0.imprint","IMPRINT",EDGE,{"derivedFrom":sQuery(id+"F0.wireOp",EDGE,"E54.rect.bottom")}),-1.0]])]});
            var Q21;
            {var subQ0=sQuery(id+"F0.wireOp",EDGE,"E51.rect.bottom");Q21=makeQuery(id+"F0.imprint","IMPRINT",FACE,{"disambiguationData":[TD([[makeQuery(id+"F0.imprint","IMPRINT",EDGE,{"derivedFrom":subQ0}),-1.0]])]});}
            var Q22;
            Q22=makeQuery(id+"F0.imprint","IMPRINT",FACE,{"disambiguationData":[TD([[makeQuery(id+"F0.imprint","IMPRINT",EDGE,{"derivedFrom":sQuery(id+"F0.wireOp",EDGE,"E53.rect.bottom")}),1.0]])]});
            extrude(context, id + "F4", {"entities" : qUnion([Q0, Q1, Q2, Q3, Q4, Q5, Q6, Q7, Q8, Q9, Q10, Q11, Q12, Q13, Q14, Q15, Q16, Q17, Q18, Q19, Q20, Q21, Q22]), "operationType" : NewBodyOperationType.REMOVE, "oppositeDirection" : true, "depth" : 2 * mm});
        }
        {
            var Q0;
            {var subQ0=sQuery(id+"F0.wireOp",EDGE,"E0.top");var subQ1=sQuery(id+"F0.wireOp",EDGE,"E0.right");Q0=makeQuery(id+"F2.boolean.opBoolean","MERGE",EDGE,{"derivedFrom":[makeQuery(id+"F1.opExtrude","SWEPT_EDGE",EDGE,{"disambiguationData":[OSD([subQ0,subQ1])]}),makeQuery(id+"F2.opExtrude","SWEPT_EDGE",EDGE,{"disambiguationData":[OSD([subQ0,subQ1])]})]});}
            var Q1;
            {var subQ0=sQuery(id+"F0.wireOp",EDGE,"E0.bottom");var subQ1=sQuery(id+"F0.wireOp",EDGE,"E0.right");Q1=makeQuery(id+"F2.boolean.opBoolean","MERGE",EDGE,{"derivedFrom":[makeQuery(id+"F1.opExtrude","SWEPT_EDGE",EDGE,{"disambiguationData":[OSD([subQ0,subQ1])]}),makeQuery(id+"F2.opExtrude","SWEPT_EDGE",EDGE,{"disambiguationData":[OSD([subQ0,subQ1])]})]});}
            var Q2;
            {var subQ0=sQuery(id+"F0.wireOp",EDGE,"E0.top");var subQ1=sQuery(id+"F0.wireOp",EDGE,"E0.left");Q2=makeQuery(id+"F2.boolean.opBoolean","MERGE",EDGE,{"derivedFrom":[makeQuery(id+"F1.opExtrude","SWEPT_EDGE",EDGE,{"disambiguationData":[OSD([subQ0,subQ1])]}),makeQuery(id+"F2.opExtrude","SWEPT_EDGE",EDGE,{"disambiguationData":[OSD([subQ0,subQ1])]})]});}
            var Q3;
            {var subQ0=sQuery(id+"F0.wireOp",EDGE,"E0.bottom");var subQ1=sQuery(id+"F0.wireOp",EDGE,"E0.left");Q3=makeQuery(id+"F2.boolean.opBoolean","MERGE",EDGE,{"derivedFrom":[makeQuery(id+"F1.opExtrude","SWEPT_EDGE",EDGE,{"disambiguationData":[OSD([subQ0,subQ1])]}),makeQuery(id+"F2.opExtrude","SWEPT_EDGE",EDGE,{"disambiguationData":[OSD([subQ0,subQ1])]})]});}
            fillet(context, id + "F5", {"entities" : qUnion([Q0, Q1, Q2, Q3]), "radius" : 6 * mm, "tangentPropagation" : true, "allowEdgeOverflow" : false});
        }
        {
            var Q0;
            Q0=makeQuery(id+"F1.opExtrude","CAP_EDGE",EDGE,{"disambiguationData":[OSD([sQuery(id+"F0.wireOp",EDGE,"E0.right")])],"isStart":false});
            chamfer(context, id + "F6", {"entities" : qUnion([Q0]), "chamferType" : ChamferType.OFFSET_ANGLE, "width" : 1 * mm, "oppositeDirection" : false, "angle" : 60 * degree, "tangentPropagation" : true});
        }
        {
            var Q0;
            Q0=qCreatedBy(makeId("Top.planeOp"),FACE);
            var sketch = newSketch(context, id + "F7", { "sketchPlane" : qUnion([Q0])});
            skLineSegment(sketch, "E74.bottom", {"start": v(-90.8, -49.72) * mm, "end": v(-38.9, -49.72) * mm});
            skLineSegment(sketch, "E74.top", {"start": v(-90.8, -21.45) * mm, "end": v(-38.9, -21.45) * mm});
            skLineSegment(sketch, "E74.left", {"start": v(-90.8, -49.72) * mm, "end": v(-90.8, -21.45) * mm});
            skLineSegment(sketch, "E74.right", {"start": v(-38.9, -49.72) * mm, "end": v(-38.9, -21.45) * mm});
            skSolve(sketch);
        }
        {
            var Q0;
            Q0=makeQuery(id+"F0.imprint","IMPRINT",FACE,{"disambiguationData":[TD([[makeQuery(id+"F0.imprint","IMPRINT",EDGE,{"derivedFrom":sQuery(id+"F0.wireOp",EDGE,"E48")}),1.0]])]});
            var Q1;
            Q1=makeQuery(id+"F0.imprint","IMPRINT",FACE,{"disambiguationData":[TD([[makeQuery(id+"F0.imprint","IMPRINT",EDGE,{"derivedFrom":sQuery(id+"F0.wireOp",EDGE,"E50")}),1.0]])]});
            var Q2;
            Q2=makeQuery(id+"F0.imprint","IMPRINT",FACE,{"disambiguationData":[TD([[makeQuery(id+"F0.imprint","IMPRINT",EDGE,{"derivedFrom":sQuery(id+"F0.wireOp",EDGE,"E35.rect.bottom")}),-1.0]])]});
            var Q3;
            Q3=makeQuery(id+"F0.imprint","IMPRINT",FACE,{"disambiguationData":[TD([[makeQuery(id+"F0.imprint","IMPRINT",EDGE,{"derivedFrom":sQuery(id+"F0.wireOp",EDGE,"E32.rect.top")}),-1.0]])]});
            var Q4;
            Q4=makeQuery(id+"F0.imprint","IMPRINT",FACE,{"disambiguationData":[TD([[makeQuery(id+"F0.imprint","IMPRINT",EDGE,{"derivedFrom":sQuery(id+"F0.wireOp",EDGE,"E49")}),1.0]])]});
            var Q5;
            Q5=makeQuery(id+"F0.imprint","IMPRINT",FACE,{"disambiguationData":[TD([[makeQuery(id+"F0.imprint","IMPRINT",EDGE,{"derivedFrom":sQuery(id+"F0.wireOp",EDGE,"E46")}),1.0]])]});
            var Q6;
            Q6=makeQuery(id+"F0.imprint","IMPRINT",FACE,{"disambiguationData":[TD([[makeQuery(id+"F0.imprint","IMPRINT",EDGE,{"derivedFrom":sQuery(id+"F0.wireOp",EDGE,"E45")}),1.0]])]});
            var Q7;
            Q7=makeQuery(id+"F0.imprint","IMPRINT",FACE,{"disambiguationData":[TD([[makeQuery(id+"F0.imprint","IMPRINT",EDGE,{"derivedFrom":sQuery(id+"F0.wireOp",EDGE,"E47")}),1.0]])]});
            extrude(context, id + "F8", {"entities" : qUnion([Q0, Q1, Q2, Q3, Q4, Q5, Q6, Q7]), "operationType" : NewBodyOperationType.ADD, "depth" : 8.25 * mm});
        }
    });
